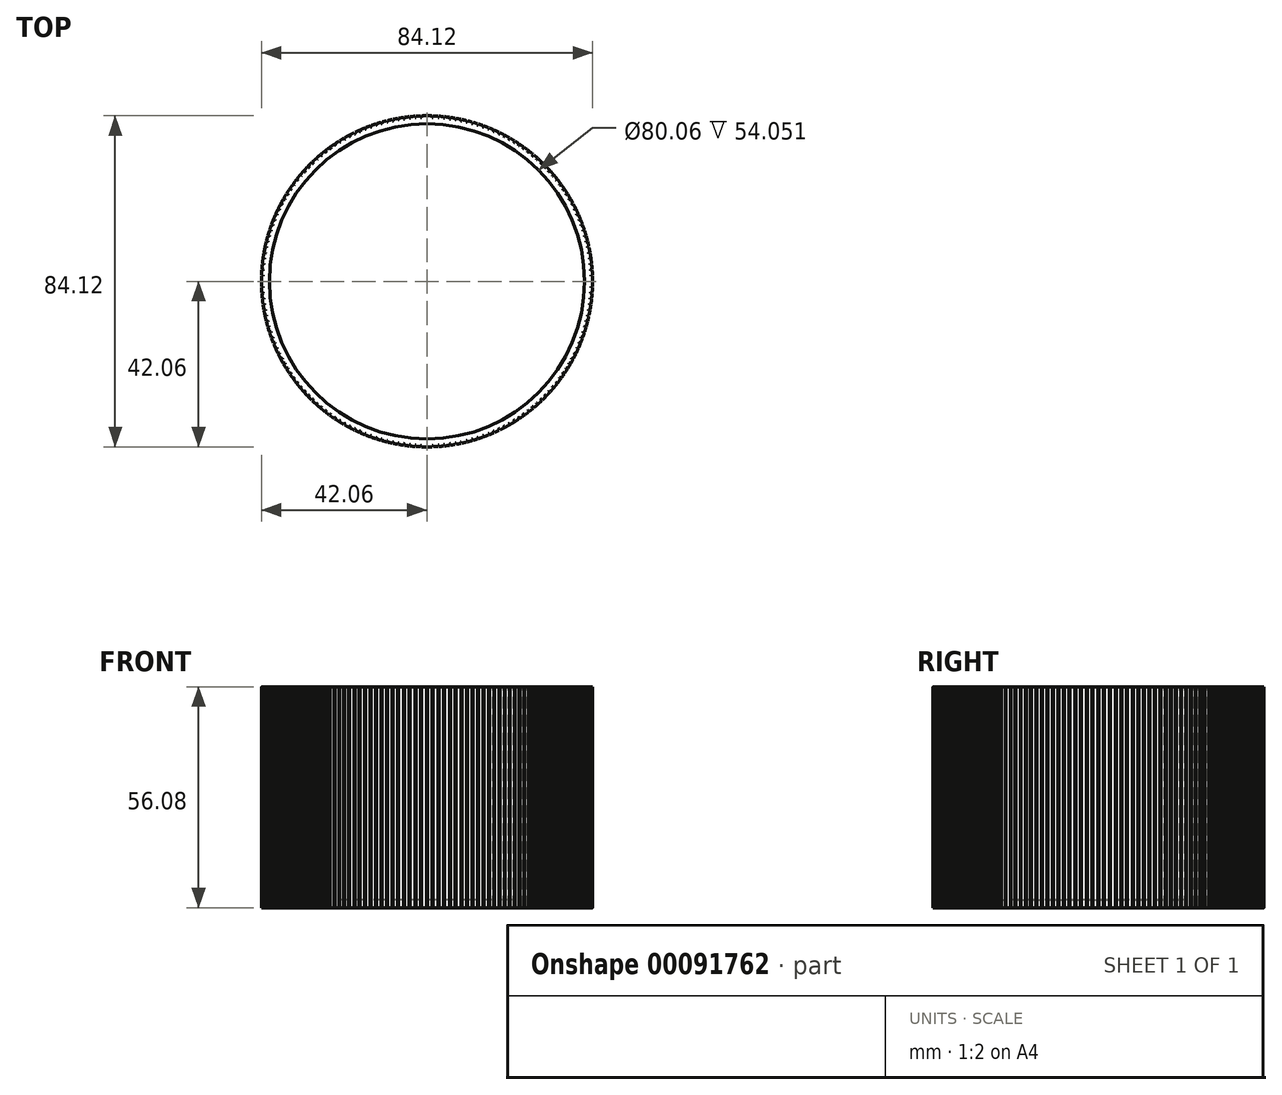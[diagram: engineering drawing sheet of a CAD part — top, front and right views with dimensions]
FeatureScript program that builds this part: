
annotation { "Feature Type Name" : "Feature", "Feature Type Description" : "" }
export const myFeature = defineFeature(function(context is Context, id is Id, definition is map)
    precondition{}
    {
        {
            var Q0;
            Q0=qCreatedBy(makeId("Top.planeOp"),FACE);
            var sketch = newSketch(context, id + "F0", { "sketchPlane" : qUnion([Q0])});
            skCircle(sketch, "E0", {"center": v(0, 0) * mm, "radius": 42.06 * mm});
            skSolve(sketch);
        }
        {
            var Q0;
            Q0 = qSketchRegion(id + "F0", true);
            extrude(context, id + "F1", {"entities" : qUnion([Q0]), "depth" : 56.08 * mm});
        }
        {
            var Q0;
            Q0=makeQuery(id+"F1.opExtrude","CAP_FACE",FACE,{"disambiguationData":[OSD([sQuery(id+"F0.wireOp",EDGE,"E0")])],"isStart":false});
            shell(context, id + "F2", {"entities" : qUnion([Q0]), "thickness" : 2.03 * mm});
        }
        {
            var Q0;
            Q0=makeQuery(id+"F1.opExtrude","CAP_FACE",FACE,{"disambiguationData":[OSD([sQuery(id+"F0.wireOp",EDGE,"E0")])],"isStart":false});
            var sketch = newSketch(context, id + "F3", { "sketchPlane" : qUnion([Q0])});
            skArc(sketch, "E1", {"start": v(0.13, 41.68) * mm, "mid": v(0, 41.68) * mm, "end": v(-0.13, 41.68) * mm});
            skLineSegment(sketch, "E2", {"start": v(-0.13, 41.68) * mm, "end": v(-0.13, 42.64) * mm});
            skLineSegment(sketch, "E3", {"start": v(-0.13, 42.64) * mm, "end": v(0.13, 42.64) * mm});
            skLineSegment(sketch, "E4", {"start": v(0.13, 42.64) * mm, "end": v(0.13, 41.68) * mm});
            skLineSegment(sketch, "E5.1.0", {"start": v(-1.58, 41.65) * mm, "end": v(-1.62, 42.6) * mm});
            skLineSegment(sketch, "E5.1.1", {"start": v(-1.36, 42.62) * mm, "end": v(-1.33, 41.66) * mm});
            skLineSegment(sketch, "E5.1.2", {"start": v(-1.62, 42.6) * mm, "end": v(-1.36, 42.62) * mm});
            skArc(sketch, "E5.1.3", {"start": v(-1.33, 41.66) * mm, "mid": v(-1.45, 41.66) * mm, "end": v(-1.58, 41.65) * mm});
            skLineSegment(sketch, "E5.2.0", {"start": v(-3.03, 41.57) * mm, "end": v(-3.1, 42.53) * mm});
            skLineSegment(sketch, "E5.2.1", {"start": v(-2.85, 42.54) * mm, "end": v(-2.78, 41.59) * mm});
            skLineSegment(sketch, "E5.2.2", {"start": v(-3.1, 42.53) * mm, "end": v(-2.85, 42.54) * mm});
            skArc(sketch, "E5.2.3", {"start": v(-2.78, 41.59) * mm, "mid": v(-2.9, 41.58) * mm, "end": v(-3.03, 41.57) * mm});
            skLineSegment(sketch, "E5.3.0", {"start": v(-4.48, 41.44) * mm, "end": v(-4.58, 42.4) * mm});
            skLineSegment(sketch, "E5.3.1", {"start": v(-4.33, 42.42) * mm, "end": v(-4.23, 41.47) * mm});
            skLineSegment(sketch, "E5.3.2", {"start": v(-4.58, 42.4) * mm, "end": v(-4.33, 42.42) * mm});
            skArc(sketch, "E5.3.3", {"start": v(-4.23, 41.47) * mm, "mid": v(-4.36, 41.45) * mm, "end": v(-4.48, 41.44) * mm});
            skLineSegment(sketch, "E5.4.0", {"start": v(-5.93, 41.26) * mm, "end": v(-6.06, 42.2) * mm});
            skLineSegment(sketch, "E5.4.1", {"start": v(-5.8, 42.24) * mm, "end": v(-5.68, 41.3) * mm});
            skLineSegment(sketch, "E5.4.2", {"start": v(-6.06, 42.2) * mm, "end": v(-5.8, 42.24) * mm});
            skArc(sketch, "E5.4.3", {"start": v(-5.68, 41.3) * mm, "mid": v(-5.8, 41.28) * mm, "end": v(-5.93, 41.26) * mm});
            skLineSegment(sketch, "E5.5.0", {"start": v(-7.36, 41.03) * mm, "end": v(-7.53, 41.97) * mm});
            skLineSegment(sketch, "E5.5.1", {"start": v(-7.28, 42.01) * mm, "end": v(-7.11, 41.07) * mm});
            skLineSegment(sketch, "E5.5.2", {"start": v(-7.53, 41.97) * mm, "end": v(-7.28, 42.01) * mm});
            skArc(sketch, "E5.5.3", {"start": v(-7.11, 41.07) * mm, "mid": v(-7.24, 41.05) * mm, "end": v(-7.36, 41.03) * mm});
            skLineSegment(sketch, "E5.6.0", {"start": v(-8.8, 40.74) * mm, "end": v(-8.99, 41.68) * mm});
            skLineSegment(sketch, "E5.6.1", {"start": v(-8.74, 41.73) * mm, "end": v(-8.54, 40.8) * mm});
            skLineSegment(sketch, "E5.6.2", {"start": v(-8.99, 41.68) * mm, "end": v(-8.74, 41.73) * mm});
            skArc(sketch, "E5.6.3", {"start": v(-8.54, 40.8) * mm, "mid": v(-8.67, 40.77) * mm, "end": v(-8.8, 40.74) * mm});
            skLineSegment(sketch, "E5.7.0", {"start": v(-10.2, 40.41) * mm, "end": v(-10.44, 41.34) * mm});
            skLineSegment(sketch, "E5.7.1", {"start": v(-10.2, 41.4) * mm, "end": v(-9.96, 40.47) * mm});
            skLineSegment(sketch, "E5.7.2", {"start": v(-10.44, 41.34) * mm, "end": v(-10.2, 41.4) * mm});
            skArc(sketch, "E5.7.3", {"start": v(-9.96, 40.47) * mm, "mid": v(-10.08, 40.44) * mm, "end": v(-10.2, 40.41) * mm});
            skLineSegment(sketch, "E5.8.0", {"start": v(-11.61, 40.03) * mm, "end": v(-11.87, 40.95) * mm});
            skLineSegment(sketch, "E5.8.1", {"start": v(-11.63, 41.02) * mm, "end": v(-11.37, 40.1) * mm});
            skLineSegment(sketch, "E5.8.2", {"start": v(-11.87, 40.95) * mm, "end": v(-11.63, 41.02) * mm});
            skArc(sketch, "E5.8.3", {"start": v(-11.37, 40.1) * mm, "mid": v(-11.49, 40.07) * mm, "end": v(-11.61, 40.03) * mm});
            skLineSegment(sketch, "E5.9.0", {"start": v(-13, 39.6) * mm, "end": v(-13.3, 40.51) * mm});
            skLineSegment(sketch, "E5.9.1", {"start": v(-13.06, 40.6) * mm, "end": v(-12.76, 39.68) * mm});
            skLineSegment(sketch, "E5.9.2", {"start": v(-13.3, 40.51) * mm, "end": v(-13.06, 40.6) * mm});
            skArc(sketch, "E5.9.3", {"start": v(-12.76, 39.68) * mm, "mid": v(-12.88, 39.64) * mm, "end": v(-13, 39.6) * mm});
            skLineSegment(sketch, "E5.10.0", {"start": v(-14.38, 39.12) * mm, "end": v(-14.7, 40.02) * mm});
            skLineSegment(sketch, "E5.10.1", {"start": v(-14.46, 40.11) * mm, "end": v(-14.14, 39.21) * mm});
            skLineSegment(sketch, "E5.10.2", {"start": v(-14.7, 40.02) * mm, "end": v(-14.46, 40.11) * mm});
            skArc(sketch, "E5.10.3", {"start": v(-14.14, 39.21) * mm, "mid": v(-14.26, 39.17) * mm, "end": v(-14.38, 39.12) * mm});
            skLineSegment(sketch, "E5.11.0", {"start": v(-15.73, 38.6) * mm, "end": v(-16.1, 39.49) * mm});
            skLineSegment(sketch, "E5.11.1", {"start": v(-15.86, 39.58) * mm, "end": v(-15.5, 38.7) * mm});
            skLineSegment(sketch, "E5.11.2", {"start": v(-16.1, 39.49) * mm, "end": v(-15.86, 39.58) * mm});
            skArc(sketch, "E5.11.3", {"start": v(-15.5, 38.7) * mm, "mid": v(-15.61, 38.65) * mm, "end": v(-15.73, 38.6) * mm});
            skLineSegment(sketch, "E5.12.0", {"start": v(-17.07, 38.03) * mm, "end": v(-17.46, 38.9) * mm});
            skLineSegment(sketch, "E5.12.1", {"start": v(-17.23, 39) * mm, "end": v(-16.84, 38.13) * mm});
            skLineSegment(sketch, "E5.12.2", {"start": v(-17.46, 38.9) * mm, "end": v(-17.23, 39) * mm});
            skArc(sketch, "E5.12.3", {"start": v(-16.84, 38.13) * mm, "mid": v(-16.95, 38.08) * mm, "end": v(-17.07, 38.03) * mm});
            skLineSegment(sketch, "E5.13.0", {"start": v(-18.39, 37.4) * mm, "end": v(-18.8, 38.27) * mm});
            skLineSegment(sketch, "E5.13.1", {"start": v(-18.58, 38.38) * mm, "end": v(-18.16, 37.52) * mm});
            skLineSegment(sketch, "E5.13.2", {"start": v(-18.8, 38.27) * mm, "end": v(-18.58, 38.38) * mm});
            skArc(sketch, "E5.13.3", {"start": v(-18.16, 37.52) * mm, "mid": v(-18.27, 37.46) * mm, "end": v(-18.39, 37.4) * mm});
            skLineSegment(sketch, "E5.14.0", {"start": v(-19.68, 36.74) * mm, "end": v(-20.13, 37.59) * mm});
            skLineSegment(sketch, "E5.14.1", {"start": v(-19.9, 37.7) * mm, "end": v(-19.46, 36.86) * mm});
            skLineSegment(sketch, "E5.14.2", {"start": v(-20.13, 37.59) * mm, "end": v(-19.9, 37.7) * mm});
            skArc(sketch, "E5.14.3", {"start": v(-19.46, 36.86) * mm, "mid": v(-19.57, 36.8) * mm, "end": v(-19.68, 36.74) * mm});
            skLineSegment(sketch, "E5.15.0", {"start": v(-20.95, 36.03) * mm, "end": v(-21.43, 36.86) * mm});
            skLineSegment(sketch, "E5.15.1", {"start": v(-21.2, 36.99) * mm, "end": v(-20.73, 36.16) * mm});
            skLineSegment(sketch, "E5.15.2", {"start": v(-21.43, 36.86) * mm, "end": v(-21.2, 36.99) * mm});
            skArc(sketch, "E5.15.3", {"start": v(-20.73, 36.16) * mm, "mid": v(-20.84, 36.1) * mm, "end": v(-20.95, 36.03) * mm});
            skLineSegment(sketch, "E5.16.0", {"start": v(-22.2, 35.28) * mm, "end": v(-22.7, 36.1) * mm});
            skLineSegment(sketch, "E5.16.1", {"start": v(-22.49, 36.23) * mm, "end": v(-21.98, 35.41) * mm});
            skLineSegment(sketch, "E5.16.2", {"start": v(-22.7, 36.1) * mm, "end": v(-22.49, 36.23) * mm});
            skArc(sketch, "E5.16.3", {"start": v(-21.98, 35.41) * mm, "mid": v(-22.09, 35.35) * mm, "end": v(-22.2, 35.28) * mm});
            skLineSegment(sketch, "E5.17.0", {"start": v(-23.41, 34.48) * mm, "end": v(-23.95, 35.28) * mm});
            skLineSegment(sketch, "E5.17.1", {"start": v(-23.74, 35.42) * mm, "end": v(-23.2, 34.63) * mm});
            skLineSegment(sketch, "E5.17.2", {"start": v(-23.95, 35.28) * mm, "end": v(-23.74, 35.42) * mm});
            skArc(sketch, "E5.17.3", {"start": v(-23.2, 34.63) * mm, "mid": v(-23.3, 34.56) * mm, "end": v(-23.41, 34.48) * mm});
            skLineSegment(sketch, "E5.18.0", {"start": v(-24.6, 33.65) * mm, "end": v(-25.17, 34.42) * mm});
            skLineSegment(sketch, "E5.18.1", {"start": v(-24.96, 34.57) * mm, "end": v(-24.4, 33.8) * mm});
            skLineSegment(sketch, "E5.18.2", {"start": v(-25.17, 34.42) * mm, "end": v(-24.96, 34.57) * mm});
            skArc(sketch, "E5.18.3", {"start": v(-24.4, 33.8) * mm, "mid": v(-24.5, 33.72) * mm, "end": v(-24.6, 33.65) * mm});
            skLineSegment(sketch, "E5.19.0", {"start": v(-25.76, 32.77) * mm, "end": v(-26.35, 33.52) * mm});
            skLineSegment(sketch, "E5.19.1", {"start": v(-26.15, 33.68) * mm, "end": v(-25.56, 32.92) * mm});
            skLineSegment(sketch, "E5.19.2", {"start": v(-26.35, 33.52) * mm, "end": v(-26.15, 33.68) * mm});
            skArc(sketch, "E5.19.3", {"start": v(-25.56, 32.92) * mm, "mid": v(-25.66, 32.85) * mm, "end": v(-25.76, 32.77) * mm});
            skLineSegment(sketch, "E5.20.0", {"start": v(-26.89, 31.85) * mm, "end": v(-27.5, 32.58) * mm});
            skLineSegment(sketch, "E5.20.1", {"start": v(-27.31, 32.74) * mm, "end": v(-26.7, 32.01) * mm});
            skLineSegment(sketch, "E5.20.2", {"start": v(-27.5, 32.58) * mm, "end": v(-27.31, 32.74) * mm});
            skArc(sketch, "E5.20.3", {"start": v(-26.7, 32.01) * mm, "mid": v(-26.8, 31.93) * mm, "end": v(-26.89, 31.85) * mm});
            skLineSegment(sketch, "E5.21.0", {"start": v(-27.98, 30.9) * mm, "end": v(-28.63, 31.6) * mm});
            skLineSegment(sketch, "E5.21.1", {"start": v(-28.44, 31.77) * mm, "end": v(-27.8, 31.06) * mm});
            skLineSegment(sketch, "E5.21.2", {"start": v(-28.63, 31.6) * mm, "end": v(-28.44, 31.77) * mm});
            skArc(sketch, "E5.21.3", {"start": v(-27.8, 31.06) * mm, "mid": v(-27.9, 30.98) * mm, "end": v(-27.98, 30.9) * mm});
            skLineSegment(sketch, "E5.22.0", {"start": v(-29.05, 29.9) * mm, "end": v(-29.71, 30.58) * mm});
            skLineSegment(sketch, "E5.22.1", {"start": v(-29.53, 30.76) * mm, "end": v(-28.86, 30.07) * mm});
            skLineSegment(sketch, "E5.22.2", {"start": v(-29.71, 30.58) * mm, "end": v(-29.53, 30.76) * mm});
            skArc(sketch, "E5.22.3", {"start": v(-28.86, 30.07) * mm, "mid": v(-28.95, 29.98) * mm, "end": v(-29.05, 29.9) * mm});
            skLineSegment(sketch, "E5.23.0", {"start": v(-30.07, 28.86) * mm, "end": v(-30.76, 29.53) * mm});
            skLineSegment(sketch, "E5.23.1", {"start": v(-30.58, 29.71) * mm, "end": v(-29.9, 29.05) * mm});
            skLineSegment(sketch, "E5.23.2", {"start": v(-30.76, 29.53) * mm, "end": v(-30.58, 29.71) * mm});
            skArc(sketch, "E5.23.3", {"start": v(-29.9, 29.05) * mm, "mid": v(-29.98, 28.95) * mm, "end": v(-30.07, 28.86) * mm});
            skLineSegment(sketch, "E5.24.0", {"start": v(-31.06, 27.8) * mm, "end": v(-31.77, 28.44) * mm});
            skLineSegment(sketch, "E5.24.1", {"start": v(-31.6, 28.63) * mm, "end": v(-30.9, 27.98) * mm});
            skLineSegment(sketch, "E5.24.2", {"start": v(-31.77, 28.44) * mm, "end": v(-31.6, 28.63) * mm});
            skArc(sketch, "E5.24.3", {"start": v(-30.9, 27.98) * mm, "mid": v(-30.98, 27.9) * mm, "end": v(-31.06, 27.8) * mm});
            skLineSegment(sketch, "E5.25.0", {"start": v(-32.01, 26.7) * mm, "end": v(-32.74, 27.31) * mm});
            skLineSegment(sketch, "E5.25.1", {"start": v(-32.58, 27.5) * mm, "end": v(-31.85, 26.89) * mm});
            skLineSegment(sketch, "E5.25.2", {"start": v(-32.74, 27.31) * mm, "end": v(-32.58, 27.5) * mm});
            skArc(sketch, "E5.25.3", {"start": v(-31.85, 26.89) * mm, "mid": v(-31.93, 26.8) * mm, "end": v(-32.01, 26.7) * mm});
            skLineSegment(sketch, "E5.26.0", {"start": v(-32.92, 25.56) * mm, "end": v(-33.68, 26.15) * mm});
            skLineSegment(sketch, "E5.26.1", {"start": v(-33.52, 26.35) * mm, "end": v(-32.77, 25.76) * mm});
            skLineSegment(sketch, "E5.26.2", {"start": v(-33.68, 26.15) * mm, "end": v(-33.52, 26.35) * mm});
            skArc(sketch, "E5.26.3", {"start": v(-32.77, 25.76) * mm, "mid": v(-32.85, 25.66) * mm, "end": v(-32.92, 25.56) * mm});
            skLineSegment(sketch, "E5.27.0", {"start": v(-33.8, 24.4) * mm, "end": v(-34.57, 24.96) * mm});
            skLineSegment(sketch, "E5.27.1", {"start": v(-34.42, 25.17) * mm, "end": v(-33.65, 24.6) * mm});
            skLineSegment(sketch, "E5.27.2", {"start": v(-34.57, 24.96) * mm, "end": v(-34.42, 25.17) * mm});
            skArc(sketch, "E5.27.3", {"start": v(-33.65, 24.6) * mm, "mid": v(-33.72, 24.5) * mm, "end": v(-33.8, 24.4) * mm});
            skLineSegment(sketch, "E5.28.0", {"start": v(-34.63, 23.2) * mm, "end": v(-35.42, 23.74) * mm});
            skLineSegment(sketch, "E5.28.1", {"start": v(-35.28, 23.95) * mm, "end": v(-34.48, 23.41) * mm});
            skLineSegment(sketch, "E5.28.2", {"start": v(-35.42, 23.74) * mm, "end": v(-35.28, 23.95) * mm});
            skArc(sketch, "E5.28.3", {"start": v(-34.48, 23.41) * mm, "mid": v(-34.56, 23.3) * mm, "end": v(-34.63, 23.2) * mm});
            skLineSegment(sketch, "E5.29.0", {"start": v(-35.41, 21.98) * mm, "end": v(-36.23, 22.49) * mm});
            skLineSegment(sketch, "E5.29.1", {"start": v(-36.1, 22.7) * mm, "end": v(-35.28, 22.2) * mm});
            skLineSegment(sketch, "E5.29.2", {"start": v(-36.23, 22.49) * mm, "end": v(-36.1, 22.7) * mm});
            skArc(sketch, "E5.29.3", {"start": v(-35.28, 22.2) * mm, "mid": v(-35.35, 22.09) * mm, "end": v(-35.41, 21.98) * mm});
            skLineSegment(sketch, "E5.30.0", {"start": v(-36.16, 20.73) * mm, "end": v(-36.99, 21.2) * mm});
            skLineSegment(sketch, "E5.30.1", {"start": v(-36.86, 21.43) * mm, "end": v(-36.03, 20.95) * mm});
            skLineSegment(sketch, "E5.30.2", {"start": v(-36.99, 21.2) * mm, "end": v(-36.86, 21.43) * mm});
            skArc(sketch, "E5.30.3", {"start": v(-36.03, 20.95) * mm, "mid": v(-36.1, 20.84) * mm, "end": v(-36.16, 20.73) * mm});
            skLineSegment(sketch, "E5.31.0", {"start": v(-36.86, 19.46) * mm, "end": v(-37.7, 19.9) * mm});
            skLineSegment(sketch, "E5.31.1", {"start": v(-37.59, 20.13) * mm, "end": v(-36.74, 19.68) * mm});
            skLineSegment(sketch, "E5.31.2", {"start": v(-37.7, 19.9) * mm, "end": v(-37.59, 20.13) * mm});
            skArc(sketch, "E5.31.3", {"start": v(-36.74, 19.68) * mm, "mid": v(-36.8, 19.57) * mm, "end": v(-36.86, 19.46) * mm});
            skLineSegment(sketch, "E5.32.0", {"start": v(-37.52, 18.16) * mm, "end": v(-38.38, 18.58) * mm});
            skLineSegment(sketch, "E5.32.1", {"start": v(-38.27, 18.8) * mm, "end": v(-37.4, 18.39) * mm});
            skLineSegment(sketch, "E5.32.2", {"start": v(-38.38, 18.58) * mm, "end": v(-38.27, 18.8) * mm});
            skArc(sketch, "E5.32.3", {"start": v(-37.4, 18.39) * mm, "mid": v(-37.46, 18.27) * mm, "end": v(-37.52, 18.16) * mm});
            skLineSegment(sketch, "E5.33.0", {"start": v(-38.13, 16.84) * mm, "end": v(-39, 17.23) * mm});
            skLineSegment(sketch, "E5.33.1", {"start": v(-38.9, 17.46) * mm, "end": v(-38.03, 17.07) * mm});
            skLineSegment(sketch, "E5.33.2", {"start": v(-39, 17.23) * mm, "end": v(-38.9, 17.46) * mm});
            skArc(sketch, "E5.33.3", {"start": v(-38.03, 17.07) * mm, "mid": v(-38.08, 16.95) * mm, "end": v(-38.13, 16.84) * mm});
            skLineSegment(sketch, "E5.34.0", {"start": v(-38.7, 15.5) * mm, "end": v(-39.58, 15.86) * mm});
            skLineSegment(sketch, "E5.34.1", {"start": v(-39.49, 16.1) * mm, "end": v(-38.6, 15.73) * mm});
            skLineSegment(sketch, "E5.34.2", {"start": v(-39.58, 15.86) * mm, "end": v(-39.49, 16.1) * mm});
            skArc(sketch, "E5.34.3", {"start": v(-38.6, 15.73) * mm, "mid": v(-38.65, 15.61) * mm, "end": v(-38.7, 15.5) * mm});
            skLineSegment(sketch, "E5.35.0", {"start": v(-39.21, 14.14) * mm, "end": v(-40.11, 14.46) * mm});
            skLineSegment(sketch, "E5.35.1", {"start": v(-40.02, 14.7) * mm, "end": v(-39.12, 14.38) * mm});
            skLineSegment(sketch, "E5.35.2", {"start": v(-40.11, 14.46) * mm, "end": v(-40.02, 14.7) * mm});
            skArc(sketch, "E5.35.3", {"start": v(-39.12, 14.38) * mm, "mid": v(-39.17, 14.26) * mm, "end": v(-39.21, 14.14) * mm});
            skLineSegment(sketch, "E5.36.0", {"start": v(-39.68, 12.76) * mm, "end": v(-40.6, 13.06) * mm});
            skLineSegment(sketch, "E5.36.1", {"start": v(-40.51, 13.3) * mm, "end": v(-39.6, 13) * mm});
            skLineSegment(sketch, "E5.36.2", {"start": v(-40.6, 13.06) * mm, "end": v(-40.51, 13.3) * mm});
            skArc(sketch, "E5.36.3", {"start": v(-39.6, 13) * mm, "mid": v(-39.64, 12.88) * mm, "end": v(-39.68, 12.76) * mm});
            skLineSegment(sketch, "E5.37.0", {"start": v(-40.1, 11.37) * mm, "end": v(-41.02, 11.63) * mm});
            skLineSegment(sketch, "E5.37.1", {"start": v(-40.95, 11.87) * mm, "end": v(-40.03, 11.61) * mm});
            skLineSegment(sketch, "E5.37.2", {"start": v(-41.02, 11.63) * mm, "end": v(-40.95, 11.87) * mm});
            skArc(sketch, "E5.37.3", {"start": v(-40.03, 11.61) * mm, "mid": v(-40.07, 11.49) * mm, "end": v(-40.1, 11.37) * mm});
            skLineSegment(sketch, "E5.38.0", {"start": v(-40.47, 9.96) * mm, "end": v(-41.4, 10.2) * mm});
            skLineSegment(sketch, "E5.38.1", {"start": v(-41.34, 10.44) * mm, "end": v(-40.41, 10.2) * mm});
            skLineSegment(sketch, "E5.38.2", {"start": v(-41.4, 10.2) * mm, "end": v(-41.34, 10.44) * mm});
            skArc(sketch, "E5.38.3", {"start": v(-40.41, 10.2) * mm, "mid": v(-40.44, 10.08) * mm, "end": v(-40.47, 9.96) * mm});
            skLineSegment(sketch, "E5.39.0", {"start": v(-40.8, 8.54) * mm, "end": v(-41.73, 8.74) * mm});
            skLineSegment(sketch, "E5.39.1", {"start": v(-41.68, 8.99) * mm, "end": v(-40.74, 8.8) * mm});
            skLineSegment(sketch, "E5.39.2", {"start": v(-41.73, 8.74) * mm, "end": v(-41.68, 8.99) * mm});
            skArc(sketch, "E5.39.3", {"start": v(-40.74, 8.8) * mm, "mid": v(-40.77, 8.67) * mm, "end": v(-40.8, 8.54) * mm});
            skLineSegment(sketch, "E5.40.0", {"start": v(-41.07, 7.11) * mm, "end": v(-42.01, 7.28) * mm});
            skLineSegment(sketch, "E5.40.1", {"start": v(-41.97, 7.53) * mm, "end": v(-41.03, 7.36) * mm});
            skLineSegment(sketch, "E5.40.2", {"start": v(-42.01, 7.28) * mm, "end": v(-41.97, 7.53) * mm});
            skArc(sketch, "E5.40.3", {"start": v(-41.03, 7.36) * mm, "mid": v(-41.05, 7.24) * mm, "end": v(-41.07, 7.11) * mm});
            skLineSegment(sketch, "E5.41.0", {"start": v(-41.3, 5.68) * mm, "end": v(-42.24, 5.8) * mm});
            skLineSegment(sketch, "E5.41.1", {"start": v(-42.2, 6.06) * mm, "end": v(-41.26, 5.93) * mm});
            skLineSegment(sketch, "E5.41.2", {"start": v(-42.24, 5.8) * mm, "end": v(-42.2, 6.06) * mm});
            skArc(sketch, "E5.41.3", {"start": v(-41.26, 5.93) * mm, "mid": v(-41.28, 5.8) * mm, "end": v(-41.3, 5.68) * mm});
            skLineSegment(sketch, "E5.42.0", {"start": v(-41.47, 4.23) * mm, "end": v(-42.42, 4.33) * mm});
            skLineSegment(sketch, "E5.42.1", {"start": v(-42.4, 4.58) * mm, "end": v(-41.44, 4.48) * mm});
            skLineSegment(sketch, "E5.42.2", {"start": v(-42.42, 4.33) * mm, "end": v(-42.4, 4.58) * mm});
            skArc(sketch, "E5.42.3", {"start": v(-41.44, 4.48) * mm, "mid": v(-41.45, 4.36) * mm, "end": v(-41.47, 4.23) * mm});
            skLineSegment(sketch, "E5.43.0", {"start": v(-41.59, 2.78) * mm, "end": v(-42.54, 2.85) * mm});
            skLineSegment(sketch, "E5.43.1", {"start": v(-42.53, 3.1) * mm, "end": v(-41.57, 3.03) * mm});
            skLineSegment(sketch, "E5.43.2", {"start": v(-42.54, 2.85) * mm, "end": v(-42.53, 3.1) * mm});
            skArc(sketch, "E5.43.3", {"start": v(-41.57, 3.03) * mm, "mid": v(-41.58, 2.9) * mm, "end": v(-41.59, 2.78) * mm});
            skLineSegment(sketch, "E5.44.0", {"start": v(-41.66, 1.33) * mm, "end": v(-42.62, 1.36) * mm});
            skLineSegment(sketch, "E5.44.1", {"start": v(-42.6, 1.62) * mm, "end": v(-41.65, 1.58) * mm});
            skLineSegment(sketch, "E5.44.2", {"start": v(-42.62, 1.36) * mm, "end": v(-42.6, 1.62) * mm});
            skArc(sketch, "E5.44.3", {"start": v(-41.65, 1.58) * mm, "mid": v(-41.66, 1.45) * mm, "end": v(-41.66, 1.33) * mm});
            skLineSegment(sketch, "E5.45.0", {"start": v(-41.68, -0.13) * mm, "end": v(-42.64, -0.13) * mm});
            skLineSegment(sketch, "E5.45.1", {"start": v(-42.64, 0.13) * mm, "end": v(-41.68, 0.13) * mm});
            skLineSegment(sketch, "E5.45.2", {"start": v(-42.64, -0.13) * mm, "end": v(-42.64, 0.13) * mm});
            skArc(sketch, "E5.45.3", {"start": v(-41.68, 0.13) * mm, "mid": v(-41.68, 0) * mm, "end": v(-41.68, -0.13) * mm});
            skLineSegment(sketch, "E5.46.0", {"start": v(-41.65, -1.58) * mm, "end": v(-42.6, -1.62) * mm});
            skLineSegment(sketch, "E5.46.1", {"start": v(-42.62, -1.36) * mm, "end": v(-41.66, -1.33) * mm});
            skLineSegment(sketch, "E5.46.2", {"start": v(-42.6, -1.62) * mm, "end": v(-42.62, -1.36) * mm});
            skArc(sketch, "E5.46.3", {"start": v(-41.66, -1.33) * mm, "mid": v(-41.66, -1.45) * mm, "end": v(-41.65, -1.58) * mm});
            skLineSegment(sketch, "E5.47.0", {"start": v(-41.57, -3.03) * mm, "end": v(-42.53, -3.1) * mm});
            skLineSegment(sketch, "E5.47.1", {"start": v(-42.54, -2.85) * mm, "end": v(-41.59, -2.78) * mm});
            skLineSegment(sketch, "E5.47.2", {"start": v(-42.53, -3.1) * mm, "end": v(-42.54, -2.85) * mm});
            skArc(sketch, "E5.47.3", {"start": v(-41.59, -2.78) * mm, "mid": v(-41.58, -2.9) * mm, "end": v(-41.57, -3.03) * mm});
            skLineSegment(sketch, "E5.48.0", {"start": v(-41.44, -4.48) * mm, "end": v(-42.4, -4.58) * mm});
            skLineSegment(sketch, "E5.48.1", {"start": v(-42.42, -4.33) * mm, "end": v(-41.47, -4.23) * mm});
            skLineSegment(sketch, "E5.48.2", {"start": v(-42.4, -4.58) * mm, "end": v(-42.42, -4.33) * mm});
            skArc(sketch, "E5.48.3", {"start": v(-41.47, -4.23) * mm, "mid": v(-41.45, -4.36) * mm, "end": v(-41.44, -4.48) * mm});
            skLineSegment(sketch, "E5.49.0", {"start": v(-41.26, -5.93) * mm, "end": v(-42.2, -6.06) * mm});
            skLineSegment(sketch, "E5.49.1", {"start": v(-42.24, -5.8) * mm, "end": v(-41.3, -5.68) * mm});
            skLineSegment(sketch, "E5.49.2", {"start": v(-42.2, -6.06) * mm, "end": v(-42.24, -5.8) * mm});
            skArc(sketch, "E5.49.3", {"start": v(-41.3, -5.68) * mm, "mid": v(-41.28, -5.8) * mm, "end": v(-41.26, -5.93) * mm});
            skLineSegment(sketch, "E5.50.0", {"start": v(-41.03, -7.36) * mm, "end": v(-41.97, -7.53) * mm});
            skLineSegment(sketch, "E5.50.1", {"start": v(-42.01, -7.28) * mm, "end": v(-41.07, -7.11) * mm});
            skLineSegment(sketch, "E5.50.2", {"start": v(-41.97, -7.53) * mm, "end": v(-42.01, -7.28) * mm});
            skArc(sketch, "E5.50.3", {"start": v(-41.07, -7.11) * mm, "mid": v(-41.05, -7.24) * mm, "end": v(-41.03, -7.36) * mm});
            skLineSegment(sketch, "E5.51.0", {"start": v(-40.74, -8.8) * mm, "end": v(-41.68, -8.99) * mm});
            skLineSegment(sketch, "E5.51.1", {"start": v(-41.73, -8.74) * mm, "end": v(-40.8, -8.54) * mm});
            skLineSegment(sketch, "E5.51.2", {"start": v(-41.68, -8.99) * mm, "end": v(-41.73, -8.74) * mm});
            skArc(sketch, "E5.51.3", {"start": v(-40.8, -8.54) * mm, "mid": v(-40.77, -8.67) * mm, "end": v(-40.74, -8.8) * mm});
            skLineSegment(sketch, "E5.52.0", {"start": v(-40.41, -10.2) * mm, "end": v(-41.34, -10.44) * mm});
            skLineSegment(sketch, "E5.52.1", {"start": v(-41.4, -10.2) * mm, "end": v(-40.47, -9.96) * mm});
            skLineSegment(sketch, "E5.52.2", {"start": v(-41.34, -10.44) * mm, "end": v(-41.4, -10.2) * mm});
            skArc(sketch, "E5.52.3", {"start": v(-40.47, -9.96) * mm, "mid": v(-40.44, -10.08) * mm, "end": v(-40.41, -10.2) * mm});
            skLineSegment(sketch, "E5.53.0", {"start": v(-40.03, -11.61) * mm, "end": v(-40.95, -11.87) * mm});
            skLineSegment(sketch, "E5.53.1", {"start": v(-41.02, -11.63) * mm, "end": v(-40.1, -11.37) * mm});
            skLineSegment(sketch, "E5.53.2", {"start": v(-40.95, -11.87) * mm, "end": v(-41.02, -11.63) * mm});
            skArc(sketch, "E5.53.3", {"start": v(-40.1, -11.37) * mm, "mid": v(-40.07, -11.49) * mm, "end": v(-40.03, -11.61) * mm});
            skLineSegment(sketch, "E5.54.0", {"start": v(-39.6, -13) * mm, "end": v(-40.51, -13.3) * mm});
            skLineSegment(sketch, "E5.54.1", {"start": v(-40.6, -13.06) * mm, "end": v(-39.68, -12.76) * mm});
            skLineSegment(sketch, "E5.54.2", {"start": v(-40.51, -13.3) * mm, "end": v(-40.6, -13.06) * mm});
            skArc(sketch, "E5.54.3", {"start": v(-39.68, -12.76) * mm, "mid": v(-39.64, -12.88) * mm, "end": v(-39.6, -13) * mm});
            skLineSegment(sketch, "E5.55.0", {"start": v(-39.12, -14.38) * mm, "end": v(-40.02, -14.7) * mm});
            skLineSegment(sketch, "E5.55.1", {"start": v(-40.11, -14.46) * mm, "end": v(-39.21, -14.14) * mm});
            skLineSegment(sketch, "E5.55.2", {"start": v(-40.02, -14.7) * mm, "end": v(-40.11, -14.46) * mm});
            skArc(sketch, "E5.55.3", {"start": v(-39.21, -14.14) * mm, "mid": v(-39.17, -14.26) * mm, "end": v(-39.12, -14.38) * mm});
            skLineSegment(sketch, "E5.56.0", {"start": v(-38.6, -15.73) * mm, "end": v(-39.49, -16.1) * mm});
            skLineSegment(sketch, "E5.56.1", {"start": v(-39.58, -15.86) * mm, "end": v(-38.7, -15.5) * mm});
            skLineSegment(sketch, "E5.56.2", {"start": v(-39.49, -16.1) * mm, "end": v(-39.58, -15.86) * mm});
            skArc(sketch, "E5.56.3", {"start": v(-38.7, -15.5) * mm, "mid": v(-38.65, -15.61) * mm, "end": v(-38.6, -15.73) * mm});
            skLineSegment(sketch, "E5.57.0", {"start": v(-38.03, -17.07) * mm, "end": v(-38.9, -17.46) * mm});
            skLineSegment(sketch, "E5.57.1", {"start": v(-39, -17.23) * mm, "end": v(-38.13, -16.84) * mm});
            skLineSegment(sketch, "E5.57.2", {"start": v(-38.9, -17.46) * mm, "end": v(-39, -17.23) * mm});
            skArc(sketch, "E5.57.3", {"start": v(-38.13, -16.84) * mm, "mid": v(-38.08, -16.95) * mm, "end": v(-38.03, -17.07) * mm});
            skLineSegment(sketch, "E5.58.0", {"start": v(-37.4, -18.39) * mm, "end": v(-38.27, -18.8) * mm});
            skLineSegment(sketch, "E5.58.1", {"start": v(-38.38, -18.58) * mm, "end": v(-37.52, -18.16) * mm});
            skLineSegment(sketch, "E5.58.2", {"start": v(-38.27, -18.8) * mm, "end": v(-38.38, -18.58) * mm});
            skArc(sketch, "E5.58.3", {"start": v(-37.52, -18.16) * mm, "mid": v(-37.46, -18.27) * mm, "end": v(-37.4, -18.39) * mm});
            skLineSegment(sketch, "E5.59.0", {"start": v(-36.74, -19.68) * mm, "end": v(-37.59, -20.13) * mm});
            skLineSegment(sketch, "E5.59.1", {"start": v(-37.7, -19.9) * mm, "end": v(-36.86, -19.46) * mm});
            skLineSegment(sketch, "E5.59.2", {"start": v(-37.59, -20.13) * mm, "end": v(-37.7, -19.9) * mm});
            skArc(sketch, "E5.59.3", {"start": v(-36.86, -19.46) * mm, "mid": v(-36.8, -19.57) * mm, "end": v(-36.74, -19.68) * mm});
            skLineSegment(sketch, "E5.60.0", {"start": v(-36.03, -20.95) * mm, "end": v(-36.86, -21.43) * mm});
            skLineSegment(sketch, "E5.60.1", {"start": v(-36.99, -21.2) * mm, "end": v(-36.16, -20.73) * mm});
            skLineSegment(sketch, "E5.60.2", {"start": v(-36.86, -21.43) * mm, "end": v(-36.99, -21.2) * mm});
            skArc(sketch, "E5.60.3", {"start": v(-36.16, -20.73) * mm, "mid": v(-36.1, -20.84) * mm, "end": v(-36.03, -20.95) * mm});
            skLineSegment(sketch, "E5.61.0", {"start": v(-35.28, -22.2) * mm, "end": v(-36.1, -22.7) * mm});
            skLineSegment(sketch, "E5.61.1", {"start": v(-36.23, -22.49) * mm, "end": v(-35.41, -21.98) * mm});
            skLineSegment(sketch, "E5.61.2", {"start": v(-36.1, -22.7) * mm, "end": v(-36.23, -22.49) * mm});
            skArc(sketch, "E5.61.3", {"start": v(-35.41, -21.98) * mm, "mid": v(-35.35, -22.09) * mm, "end": v(-35.28, -22.2) * mm});
            skLineSegment(sketch, "E5.62.0", {"start": v(-34.48, -23.41) * mm, "end": v(-35.28, -23.95) * mm});
            skLineSegment(sketch, "E5.62.1", {"start": v(-35.42, -23.74) * mm, "end": v(-34.63, -23.2) * mm});
            skLineSegment(sketch, "E5.62.2", {"start": v(-35.28, -23.95) * mm, "end": v(-35.42, -23.74) * mm});
            skArc(sketch, "E5.62.3", {"start": v(-34.63, -23.2) * mm, "mid": v(-34.56, -23.3) * mm, "end": v(-34.48, -23.41) * mm});
            skLineSegment(sketch, "E5.63.0", {"start": v(-33.65, -24.6) * mm, "end": v(-34.42, -25.17) * mm});
            skLineSegment(sketch, "E5.63.1", {"start": v(-34.57, -24.96) * mm, "end": v(-33.8, -24.4) * mm});
            skLineSegment(sketch, "E5.63.2", {"start": v(-34.42, -25.17) * mm, "end": v(-34.57, -24.96) * mm});
            skArc(sketch, "E5.63.3", {"start": v(-33.8, -24.4) * mm, "mid": v(-33.72, -24.5) * mm, "end": v(-33.65, -24.6) * mm});
            skLineSegment(sketch, "E5.64.0", {"start": v(-32.77, -25.76) * mm, "end": v(-33.52, -26.35) * mm});
            skLineSegment(sketch, "E5.64.1", {"start": v(-33.68, -26.15) * mm, "end": v(-32.92, -25.56) * mm});
            skLineSegment(sketch, "E5.64.2", {"start": v(-33.52, -26.35) * mm, "end": v(-33.68, -26.15) * mm});
            skArc(sketch, "E5.64.3", {"start": v(-32.92, -25.56) * mm, "mid": v(-32.85, -25.66) * mm, "end": v(-32.77, -25.76) * mm});
            skLineSegment(sketch, "E5.65.0", {"start": v(-31.85, -26.89) * mm, "end": v(-32.58, -27.5) * mm});
            skLineSegment(sketch, "E5.65.1", {"start": v(-32.74, -27.31) * mm, "end": v(-32.01, -26.7) * mm});
            skLineSegment(sketch, "E5.65.2", {"start": v(-32.58, -27.5) * mm, "end": v(-32.74, -27.31) * mm});
            skArc(sketch, "E5.65.3", {"start": v(-32.01, -26.7) * mm, "mid": v(-31.93, -26.8) * mm, "end": v(-31.85, -26.89) * mm});
            skLineSegment(sketch, "E5.66.0", {"start": v(-30.9, -27.98) * mm, "end": v(-31.6, -28.63) * mm});
            skLineSegment(sketch, "E5.66.1", {"start": v(-31.77, -28.44) * mm, "end": v(-31.06, -27.8) * mm});
            skLineSegment(sketch, "E5.66.2", {"start": v(-31.6, -28.63) * mm, "end": v(-31.77, -28.44) * mm});
            skArc(sketch, "E5.66.3", {"start": v(-31.06, -27.8) * mm, "mid": v(-30.98, -27.9) * mm, "end": v(-30.9, -27.98) * mm});
            skLineSegment(sketch, "E5.67.0", {"start": v(-29.9, -29.05) * mm, "end": v(-30.58, -29.71) * mm});
            skLineSegment(sketch, "E5.67.1", {"start": v(-30.76, -29.53) * mm, "end": v(-30.07, -28.86) * mm});
            skLineSegment(sketch, "E5.67.2", {"start": v(-30.58, -29.71) * mm, "end": v(-30.76, -29.53) * mm});
            skArc(sketch, "E5.67.3", {"start": v(-30.07, -28.86) * mm, "mid": v(-29.98, -28.95) * mm, "end": v(-29.9, -29.05) * mm});
            skLineSegment(sketch, "E5.68.0", {"start": v(-28.86, -30.07) * mm, "end": v(-29.53, -30.76) * mm});
            skLineSegment(sketch, "E5.68.1", {"start": v(-29.71, -30.58) * mm, "end": v(-29.05, -29.9) * mm});
            skLineSegment(sketch, "E5.68.2", {"start": v(-29.53, -30.76) * mm, "end": v(-29.71, -30.58) * mm});
            skArc(sketch, "E5.68.3", {"start": v(-29.05, -29.9) * mm, "mid": v(-28.95, -29.98) * mm, "end": v(-28.86, -30.07) * mm});
            skLineSegment(sketch, "E5.69.0", {"start": v(-27.8, -31.06) * mm, "end": v(-28.44, -31.77) * mm});
            skLineSegment(sketch, "E5.69.1", {"start": v(-28.63, -31.6) * mm, "end": v(-27.98, -30.9) * mm});
            skLineSegment(sketch, "E5.69.2", {"start": v(-28.44, -31.77) * mm, "end": v(-28.63, -31.6) * mm});
            skArc(sketch, "E5.69.3", {"start": v(-27.98, -30.9) * mm, "mid": v(-27.9, -30.98) * mm, "end": v(-27.8, -31.06) * mm});
            skLineSegment(sketch, "E5.70.0", {"start": v(-26.7, -32.01) * mm, "end": v(-27.31, -32.74) * mm});
            skLineSegment(sketch, "E5.70.1", {"start": v(-27.5, -32.58) * mm, "end": v(-26.89, -31.85) * mm});
            skLineSegment(sketch, "E5.70.2", {"start": v(-27.31, -32.74) * mm, "end": v(-27.5, -32.58) * mm});
            skArc(sketch, "E5.70.3", {"start": v(-26.89, -31.85) * mm, "mid": v(-26.8, -31.93) * mm, "end": v(-26.7, -32.01) * mm});
            skLineSegment(sketch, "E5.71.0", {"start": v(-25.56, -32.92) * mm, "end": v(-26.15, -33.68) * mm});
            skLineSegment(sketch, "E5.71.1", {"start": v(-26.35, -33.52) * mm, "end": v(-25.76, -32.77) * mm});
            skLineSegment(sketch, "E5.71.2", {"start": v(-26.15, -33.68) * mm, "end": v(-26.35, -33.52) * mm});
            skArc(sketch, "E5.71.3", {"start": v(-25.76, -32.77) * mm, "mid": v(-25.66, -32.85) * mm, "end": v(-25.56, -32.92) * mm});
            skLineSegment(sketch, "E5.72.0", {"start": v(-24.4, -33.8) * mm, "end": v(-24.96, -34.57) * mm});
            skLineSegment(sketch, "E5.72.1", {"start": v(-25.17, -34.42) * mm, "end": v(-24.6, -33.65) * mm});
            skLineSegment(sketch, "E5.72.2", {"start": v(-24.96, -34.57) * mm, "end": v(-25.17, -34.42) * mm});
            skArc(sketch, "E5.72.3", {"start": v(-24.6, -33.65) * mm, "mid": v(-24.5, -33.72) * mm, "end": v(-24.4, -33.8) * mm});
            skLineSegment(sketch, "E5.73.0", {"start": v(-23.2, -34.63) * mm, "end": v(-23.74, -35.42) * mm});
            skLineSegment(sketch, "E5.73.1", {"start": v(-23.95, -35.28) * mm, "end": v(-23.41, -34.48) * mm});
            skLineSegment(sketch, "E5.73.2", {"start": v(-23.74, -35.42) * mm, "end": v(-23.95, -35.28) * mm});
            skArc(sketch, "E5.73.3", {"start": v(-23.41, -34.48) * mm, "mid": v(-23.3, -34.56) * mm, "end": v(-23.2, -34.63) * mm});
            skLineSegment(sketch, "E5.74.0", {"start": v(-21.98, -35.41) * mm, "end": v(-22.49, -36.23) * mm});
            skLineSegment(sketch, "E5.74.1", {"start": v(-22.7, -36.1) * mm, "end": v(-22.2, -35.28) * mm});
            skLineSegment(sketch, "E5.74.2", {"start": v(-22.49, -36.23) * mm, "end": v(-22.7, -36.1) * mm});
            skArc(sketch, "E5.74.3", {"start": v(-22.2, -35.28) * mm, "mid": v(-22.09, -35.35) * mm, "end": v(-21.98, -35.41) * mm});
            skLineSegment(sketch, "E5.75.0", {"start": v(-20.73, -36.16) * mm, "end": v(-21.2, -36.99) * mm});
            skLineSegment(sketch, "E5.75.1", {"start": v(-21.43, -36.86) * mm, "end": v(-20.95, -36.03) * mm});
            skLineSegment(sketch, "E5.75.2", {"start": v(-21.2, -36.99) * mm, "end": v(-21.43, -36.86) * mm});
            skArc(sketch, "E5.75.3", {"start": v(-20.95, -36.03) * mm, "mid": v(-20.84, -36.1) * mm, "end": v(-20.73, -36.16) * mm});
            skLineSegment(sketch, "E5.76.0", {"start": v(-19.46, -36.86) * mm, "end": v(-19.9, -37.7) * mm});
            skLineSegment(sketch, "E5.76.1", {"start": v(-20.13, -37.59) * mm, "end": v(-19.68, -36.74) * mm});
            skLineSegment(sketch, "E5.76.2", {"start": v(-19.9, -37.7) * mm, "end": v(-20.13, -37.59) * mm});
            skArc(sketch, "E5.76.3", {"start": v(-19.68, -36.74) * mm, "mid": v(-19.57, -36.8) * mm, "end": v(-19.46, -36.86) * mm});
            skLineSegment(sketch, "E5.77.0", {"start": v(-18.16, -37.52) * mm, "end": v(-18.58, -38.38) * mm});
            skLineSegment(sketch, "E5.77.1", {"start": v(-18.8, -38.27) * mm, "end": v(-18.39, -37.4) * mm});
            skLineSegment(sketch, "E5.77.2", {"start": v(-18.58, -38.38) * mm, "end": v(-18.8, -38.27) * mm});
            skArc(sketch, "E5.77.3", {"start": v(-18.39, -37.4) * mm, "mid": v(-18.27, -37.46) * mm, "end": v(-18.16, -37.52) * mm});
            skLineSegment(sketch, "E5.78.0", {"start": v(-16.84, -38.13) * mm, "end": v(-17.23, -39) * mm});
            skLineSegment(sketch, "E5.78.1", {"start": v(-17.46, -38.9) * mm, "end": v(-17.07, -38.03) * mm});
            skLineSegment(sketch, "E5.78.2", {"start": v(-17.23, -39) * mm, "end": v(-17.46, -38.9) * mm});
            skArc(sketch, "E5.78.3", {"start": v(-17.07, -38.03) * mm, "mid": v(-16.95, -38.08) * mm, "end": v(-16.84, -38.13) * mm});
            skLineSegment(sketch, "E5.79.0", {"start": v(-15.5, -38.7) * mm, "end": v(-15.86, -39.58) * mm});
            skLineSegment(sketch, "E5.79.1", {"start": v(-16.1, -39.49) * mm, "end": v(-15.73, -38.6) * mm});
            skLineSegment(sketch, "E5.79.2", {"start": v(-15.86, -39.58) * mm, "end": v(-16.1, -39.49) * mm});
            skArc(sketch, "E5.79.3", {"start": v(-15.73, -38.6) * mm, "mid": v(-15.61, -38.65) * mm, "end": v(-15.5, -38.7) * mm});
            skLineSegment(sketch, "E5.80.0", {"start": v(-14.14, -39.21) * mm, "end": v(-14.46, -40.11) * mm});
            skLineSegment(sketch, "E5.80.1", {"start": v(-14.7, -40.02) * mm, "end": v(-14.38, -39.12) * mm});
            skLineSegment(sketch, "E5.80.2", {"start": v(-14.46, -40.11) * mm, "end": v(-14.7, -40.02) * mm});
            skArc(sketch, "E5.80.3", {"start": v(-14.38, -39.12) * mm, "mid": v(-14.26, -39.17) * mm, "end": v(-14.14, -39.21) * mm});
            skLineSegment(sketch, "E5.81.0", {"start": v(-12.76, -39.68) * mm, "end": v(-13.06, -40.6) * mm});
            skLineSegment(sketch, "E5.81.1", {"start": v(-13.3, -40.51) * mm, "end": v(-13, -39.6) * mm});
            skLineSegment(sketch, "E5.81.2", {"start": v(-13.06, -40.6) * mm, "end": v(-13.3, -40.51) * mm});
            skArc(sketch, "E5.81.3", {"start": v(-13, -39.6) * mm, "mid": v(-12.88, -39.64) * mm, "end": v(-12.76, -39.68) * mm});
            skLineSegment(sketch, "E5.82.0", {"start": v(-11.37, -40.1) * mm, "end": v(-11.63, -41.02) * mm});
            skLineSegment(sketch, "E5.82.1", {"start": v(-11.87, -40.95) * mm, "end": v(-11.61, -40.03) * mm});
            skLineSegment(sketch, "E5.82.2", {"start": v(-11.63, -41.02) * mm, "end": v(-11.87, -40.95) * mm});
            skArc(sketch, "E5.82.3", {"start": v(-11.61, -40.03) * mm, "mid": v(-11.49, -40.07) * mm, "end": v(-11.37, -40.1) * mm});
            skLineSegment(sketch, "E5.83.0", {"start": v(-9.96, -40.47) * mm, "end": v(-10.2, -41.4) * mm});
            skLineSegment(sketch, "E5.83.1", {"start": v(-10.44, -41.34) * mm, "end": v(-10.2, -40.41) * mm});
            skLineSegment(sketch, "E5.83.2", {"start": v(-10.2, -41.4) * mm, "end": v(-10.44, -41.34) * mm});
            skArc(sketch, "E5.83.3", {"start": v(-10.2, -40.41) * mm, "mid": v(-10.08, -40.44) * mm, "end": v(-9.96, -40.47) * mm});
            skLineSegment(sketch, "E5.84.0", {"start": v(-8.54, -40.8) * mm, "end": v(-8.74, -41.73) * mm});
            skLineSegment(sketch, "E5.84.1", {"start": v(-8.99, -41.68) * mm, "end": v(-8.8, -40.74) * mm});
            skLineSegment(sketch, "E5.84.2", {"start": v(-8.74, -41.73) * mm, "end": v(-8.99, -41.68) * mm});
            skArc(sketch, "E5.84.3", {"start": v(-8.8, -40.74) * mm, "mid": v(-8.67, -40.77) * mm, "end": v(-8.54, -40.8) * mm});
            skLineSegment(sketch, "E5.85.0", {"start": v(-7.11, -41.07) * mm, "end": v(-7.28, -42.01) * mm});
            skLineSegment(sketch, "E5.85.1", {"start": v(-7.53, -41.97) * mm, "end": v(-7.36, -41.03) * mm});
            skLineSegment(sketch, "E5.85.2", {"start": v(-7.28, -42.01) * mm, "end": v(-7.53, -41.97) * mm});
            skArc(sketch, "E5.85.3", {"start": v(-7.36, -41.03) * mm, "mid": v(-7.24, -41.05) * mm, "end": v(-7.11, -41.07) * mm});
            skLineSegment(sketch, "E5.86.0", {"start": v(-5.68, -41.3) * mm, "end": v(-5.8, -42.24) * mm});
            skLineSegment(sketch, "E5.86.1", {"start": v(-6.06, -42.2) * mm, "end": v(-5.93, -41.26) * mm});
            skLineSegment(sketch, "E5.86.2", {"start": v(-5.8, -42.24) * mm, "end": v(-6.06, -42.2) * mm});
            skArc(sketch, "E5.86.3", {"start": v(-5.93, -41.26) * mm, "mid": v(-5.8, -41.28) * mm, "end": v(-5.68, -41.3) * mm});
            skLineSegment(sketch, "E5.87.0", {"start": v(-4.23, -41.47) * mm, "end": v(-4.33, -42.42) * mm});
            skLineSegment(sketch, "E5.87.1", {"start": v(-4.58, -42.4) * mm, "end": v(-4.48, -41.44) * mm});
            skLineSegment(sketch, "E5.87.2", {"start": v(-4.33, -42.42) * mm, "end": v(-4.58, -42.4) * mm});
            skArc(sketch, "E5.87.3", {"start": v(-4.48, -41.44) * mm, "mid": v(-4.36, -41.45) * mm, "end": v(-4.23, -41.47) * mm});
            skLineSegment(sketch, "E5.88.0", {"start": v(-2.78, -41.59) * mm, "end": v(-2.85, -42.54) * mm});
            skLineSegment(sketch, "E5.88.1", {"start": v(-3.1, -42.53) * mm, "end": v(-3.03, -41.57) * mm});
            skLineSegment(sketch, "E5.88.2", {"start": v(-2.85, -42.54) * mm, "end": v(-3.1, -42.53) * mm});
            skArc(sketch, "E5.88.3", {"start": v(-3.03, -41.57) * mm, "mid": v(-2.9, -41.58) * mm, "end": v(-2.78, -41.59) * mm});
            skLineSegment(sketch, "E5.89.0", {"start": v(-1.33, -41.66) * mm, "end": v(-1.36, -42.62) * mm});
            skLineSegment(sketch, "E5.89.1", {"start": v(-1.62, -42.6) * mm, "end": v(-1.58, -41.65) * mm});
            skLineSegment(sketch, "E5.89.2", {"start": v(-1.36, -42.62) * mm, "end": v(-1.62, -42.6) * mm});
            skArc(sketch, "E5.89.3", {"start": v(-1.58, -41.65) * mm, "mid": v(-1.45, -41.66) * mm, "end": v(-1.33, -41.66) * mm});
            skLineSegment(sketch, "E5.90.0", {"start": v(0.13, -41.68) * mm, "end": v(0.13, -42.64) * mm});
            skLineSegment(sketch, "E5.90.1", {"start": v(-0.13, -42.64) * mm, "end": v(-0.13, -41.68) * mm});
            skLineSegment(sketch, "E5.90.2", {"start": v(0.13, -42.64) * mm, "end": v(-0.13, -42.64) * mm});
            skArc(sketch, "E5.90.3", {"start": v(-0.13, -41.68) * mm, "mid": v(0, -41.68) * mm, "end": v(0.13, -41.68) * mm});
            skLineSegment(sketch, "E5.91.0", {"start": v(1.58, -41.65) * mm, "end": v(1.62, -42.6) * mm});
            skLineSegment(sketch, "E5.91.1", {"start": v(1.36, -42.62) * mm, "end": v(1.33, -41.66) * mm});
            skLineSegment(sketch, "E5.91.2", {"start": v(1.62, -42.6) * mm, "end": v(1.36, -42.62) * mm});
            skArc(sketch, "E5.91.3", {"start": v(1.33, -41.66) * mm, "mid": v(1.45, -41.66) * mm, "end": v(1.58, -41.65) * mm});
            skLineSegment(sketch, "E5.92.0", {"start": v(3.03, -41.57) * mm, "end": v(3.1, -42.53) * mm});
            skLineSegment(sketch, "E5.92.1", {"start": v(2.85, -42.54) * mm, "end": v(2.78, -41.59) * mm});
            skLineSegment(sketch, "E5.92.2", {"start": v(3.1, -42.53) * mm, "end": v(2.85, -42.54) * mm});
            skArc(sketch, "E5.92.3", {"start": v(2.78, -41.59) * mm, "mid": v(2.9, -41.58) * mm, "end": v(3.03, -41.57) * mm});
            skLineSegment(sketch, "E5.93.0", {"start": v(4.48, -41.44) * mm, "end": v(4.58, -42.4) * mm});
            skLineSegment(sketch, "E5.93.1", {"start": v(4.33, -42.42) * mm, "end": v(4.23, -41.47) * mm});
            skLineSegment(sketch, "E5.93.2", {"start": v(4.58, -42.4) * mm, "end": v(4.33, -42.42) * mm});
            skArc(sketch, "E5.93.3", {"start": v(4.23, -41.47) * mm, "mid": v(4.36, -41.45) * mm, "end": v(4.48, -41.44) * mm});
            skLineSegment(sketch, "E5.94.0", {"start": v(5.93, -41.26) * mm, "end": v(6.06, -42.2) * mm});
            skLineSegment(sketch, "E5.94.1", {"start": v(5.8, -42.24) * mm, "end": v(5.68, -41.3) * mm});
            skLineSegment(sketch, "E5.94.2", {"start": v(6.06, -42.2) * mm, "end": v(5.8, -42.24) * mm});
            skArc(sketch, "E5.94.3", {"start": v(5.68, -41.3) * mm, "mid": v(5.8, -41.28) * mm, "end": v(5.93, -41.26) * mm});
            skLineSegment(sketch, "E5.95.0", {"start": v(7.36, -41.03) * mm, "end": v(7.53, -41.97) * mm});
            skLineSegment(sketch, "E5.95.1", {"start": v(7.28, -42.01) * mm, "end": v(7.11, -41.07) * mm});
            skLineSegment(sketch, "E5.95.2", {"start": v(7.53, -41.97) * mm, "end": v(7.28, -42.01) * mm});
            skArc(sketch, "E5.95.3", {"start": v(7.11, -41.07) * mm, "mid": v(7.24, -41.05) * mm, "end": v(7.36, -41.03) * mm});
            skLineSegment(sketch, "E5.96.0", {"start": v(8.8, -40.74) * mm, "end": v(8.99, -41.68) * mm});
            skLineSegment(sketch, "E5.96.1", {"start": v(8.74, -41.73) * mm, "end": v(8.54, -40.8) * mm});
            skLineSegment(sketch, "E5.96.2", {"start": v(8.99, -41.68) * mm, "end": v(8.74, -41.73) * mm});
            skArc(sketch, "E5.96.3", {"start": v(8.54, -40.8) * mm, "mid": v(8.67, -40.77) * mm, "end": v(8.8, -40.74) * mm});
            skLineSegment(sketch, "E5.97.0", {"start": v(10.2, -40.41) * mm, "end": v(10.44, -41.34) * mm});
            skLineSegment(sketch, "E5.97.1", {"start": v(10.2, -41.4) * mm, "end": v(9.96, -40.47) * mm});
            skLineSegment(sketch, "E5.97.2", {"start": v(10.44, -41.34) * mm, "end": v(10.2, -41.4) * mm});
            skArc(sketch, "E5.97.3", {"start": v(9.96, -40.47) * mm, "mid": v(10.08, -40.44) * mm, "end": v(10.2, -40.41) * mm});
            skLineSegment(sketch, "E5.98.0", {"start": v(11.61, -40.03) * mm, "end": v(11.87, -40.95) * mm});
            skLineSegment(sketch, "E5.98.1", {"start": v(11.63, -41.02) * mm, "end": v(11.37, -40.1) * mm});
            skLineSegment(sketch, "E5.98.2", {"start": v(11.87, -40.95) * mm, "end": v(11.63, -41.02) * mm});
            skArc(sketch, "E5.98.3", {"start": v(11.37, -40.1) * mm, "mid": v(11.49, -40.07) * mm, "end": v(11.61, -40.03) * mm});
            skLineSegment(sketch, "E5.99.0", {"start": v(13, -39.6) * mm, "end": v(13.3, -40.51) * mm});
            skLineSegment(sketch, "E5.99.1", {"start": v(13.06, -40.6) * mm, "end": v(12.76, -39.68) * mm});
            skLineSegment(sketch, "E5.99.2", {"start": v(13.3, -40.51) * mm, "end": v(13.06, -40.6) * mm});
            skArc(sketch, "E5.99.3", {"start": v(12.76, -39.68) * mm, "mid": v(12.88, -39.64) * mm, "end": v(13, -39.6) * mm});
            skLineSegment(sketch, "E5.100.0", {"start": v(14.38, -39.12) * mm, "end": v(14.7, -40.02) * mm});
            skLineSegment(sketch, "E5.100.1", {"start": v(14.46, -40.11) * mm, "end": v(14.14, -39.21) * mm});
            skLineSegment(sketch, "E5.100.2", {"start": v(14.7, -40.02) * mm, "end": v(14.46, -40.11) * mm});
            skArc(sketch, "E5.100.3", {"start": v(14.14, -39.21) * mm, "mid": v(14.26, -39.17) * mm, "end": v(14.38, -39.12) * mm});
            skLineSegment(sketch, "E5.101.0", {"start": v(15.73, -38.6) * mm, "end": v(16.1, -39.49) * mm});
            skLineSegment(sketch, "E5.101.1", {"start": v(15.86, -39.58) * mm, "end": v(15.5, -38.7) * mm});
            skLineSegment(sketch, "E5.101.2", {"start": v(16.1, -39.49) * mm, "end": v(15.86, -39.58) * mm});
            skArc(sketch, "E5.101.3", {"start": v(15.5, -38.7) * mm, "mid": v(15.61, -38.65) * mm, "end": v(15.73, -38.6) * mm});
            skLineSegment(sketch, "E5.102.0", {"start": v(17.07, -38.03) * mm, "end": v(17.46, -38.9) * mm});
            skLineSegment(sketch, "E5.102.1", {"start": v(17.23, -39) * mm, "end": v(16.84, -38.13) * mm});
            skLineSegment(sketch, "E5.102.2", {"start": v(17.46, -38.9) * mm, "end": v(17.23, -39) * mm});
            skArc(sketch, "E5.102.3", {"start": v(16.84, -38.13) * mm, "mid": v(16.95, -38.08) * mm, "end": v(17.07, -38.03) * mm});
            skLineSegment(sketch, "E5.103.0", {"start": v(18.39, -37.4) * mm, "end": v(18.8, -38.27) * mm});
            skLineSegment(sketch, "E5.103.1", {"start": v(18.58, -38.38) * mm, "end": v(18.16, -37.52) * mm});
            skLineSegment(sketch, "E5.103.2", {"start": v(18.8, -38.27) * mm, "end": v(18.58, -38.38) * mm});
            skArc(sketch, "E5.103.3", {"start": v(18.16, -37.52) * mm, "mid": v(18.27, -37.46) * mm, "end": v(18.39, -37.4) * mm});
            skLineSegment(sketch, "E5.104.0", {"start": v(19.68, -36.74) * mm, "end": v(20.13, -37.59) * mm});
            skLineSegment(sketch, "E5.104.1", {"start": v(19.9, -37.7) * mm, "end": v(19.46, -36.86) * mm});
            skLineSegment(sketch, "E5.104.2", {"start": v(20.13, -37.59) * mm, "end": v(19.9, -37.7) * mm});
            skArc(sketch, "E5.104.3", {"start": v(19.46, -36.86) * mm, "mid": v(19.57, -36.8) * mm, "end": v(19.68, -36.74) * mm});
            skLineSegment(sketch, "E5.105.0", {"start": v(20.95, -36.03) * mm, "end": v(21.43, -36.86) * mm});
            skLineSegment(sketch, "E5.105.1", {"start": v(21.2, -36.99) * mm, "end": v(20.73, -36.16) * mm});
            skLineSegment(sketch, "E5.105.2", {"start": v(21.43, -36.86) * mm, "end": v(21.2, -36.99) * mm});
            skArc(sketch, "E5.105.3", {"start": v(20.73, -36.16) * mm, "mid": v(20.84, -36.1) * mm, "end": v(20.95, -36.03) * mm});
            skLineSegment(sketch, "E5.106.0", {"start": v(22.2, -35.28) * mm, "end": v(22.7, -36.1) * mm});
            skLineSegment(sketch, "E5.106.1", {"start": v(22.49, -36.23) * mm, "end": v(21.98, -35.41) * mm});
            skLineSegment(sketch, "E5.106.2", {"start": v(22.7, -36.1) * mm, "end": v(22.49, -36.23) * mm});
            skArc(sketch, "E5.106.3", {"start": v(21.98, -35.41) * mm, "mid": v(22.09, -35.35) * mm, "end": v(22.2, -35.28) * mm});
            skLineSegment(sketch, "E5.107.0", {"start": v(23.41, -34.48) * mm, "end": v(23.95, -35.28) * mm});
            skLineSegment(sketch, "E5.107.1", {"start": v(23.74, -35.42) * mm, "end": v(23.2, -34.63) * mm});
            skLineSegment(sketch, "E5.107.2", {"start": v(23.95, -35.28) * mm, "end": v(23.74, -35.42) * mm});
            skArc(sketch, "E5.107.3", {"start": v(23.2, -34.63) * mm, "mid": v(23.3, -34.56) * mm, "end": v(23.41, -34.48) * mm});
            skLineSegment(sketch, "E5.108.0", {"start": v(24.6, -33.65) * mm, "end": v(25.17, -34.42) * mm});
            skLineSegment(sketch, "E5.108.1", {"start": v(24.96, -34.57) * mm, "end": v(24.4, -33.8) * mm});
            skLineSegment(sketch, "E5.108.2", {"start": v(25.17, -34.42) * mm, "end": v(24.96, -34.57) * mm});
            skArc(sketch, "E5.108.3", {"start": v(24.4, -33.8) * mm, "mid": v(24.5, -33.72) * mm, "end": v(24.6, -33.65) * mm});
            skLineSegment(sketch, "E5.109.0", {"start": v(25.76, -32.77) * mm, "end": v(26.35, -33.52) * mm});
            skLineSegment(sketch, "E5.109.1", {"start": v(26.15, -33.68) * mm, "end": v(25.56, -32.92) * mm});
            skLineSegment(sketch, "E5.109.2", {"start": v(26.35, -33.52) * mm, "end": v(26.15, -33.68) * mm});
            skArc(sketch, "E5.109.3", {"start": v(25.56, -32.92) * mm, "mid": v(25.66, -32.85) * mm, "end": v(25.76, -32.77) * mm});
            skLineSegment(sketch, "E5.110.0", {"start": v(26.89, -31.85) * mm, "end": v(27.5, -32.58) * mm});
            skLineSegment(sketch, "E5.110.1", {"start": v(27.31, -32.74) * mm, "end": v(26.7, -32.01) * mm});
            skLineSegment(sketch, "E5.110.2", {"start": v(27.5, -32.58) * mm, "end": v(27.31, -32.74) * mm});
            skArc(sketch, "E5.110.3", {"start": v(26.7, -32.01) * mm, "mid": v(26.8, -31.93) * mm, "end": v(26.89, -31.85) * mm});
            skLineSegment(sketch, "E5.111.0", {"start": v(27.98, -30.9) * mm, "end": v(28.63, -31.6) * mm});
            skLineSegment(sketch, "E5.111.1", {"start": v(28.44, -31.77) * mm, "end": v(27.8, -31.06) * mm});
            skLineSegment(sketch, "E5.111.2", {"start": v(28.63, -31.6) * mm, "end": v(28.44, -31.77) * mm});
            skArc(sketch, "E5.111.3", {"start": v(27.8, -31.06) * mm, "mid": v(27.9, -30.98) * mm, "end": v(27.98, -30.9) * mm});
            skLineSegment(sketch, "E5.112.0", {"start": v(29.05, -29.9) * mm, "end": v(29.71, -30.58) * mm});
            skLineSegment(sketch, "E5.112.1", {"start": v(29.53, -30.76) * mm, "end": v(28.86, -30.07) * mm});
            skLineSegment(sketch, "E5.112.2", {"start": v(29.71, -30.58) * mm, "end": v(29.53, -30.76) * mm});
            skArc(sketch, "E5.112.3", {"start": v(28.86, -30.07) * mm, "mid": v(28.95, -29.98) * mm, "end": v(29.05, -29.9) * mm});
            skLineSegment(sketch, "E5.113.0", {"start": v(30.07, -28.86) * mm, "end": v(30.76, -29.53) * mm});
            skLineSegment(sketch, "E5.113.1", {"start": v(30.58, -29.71) * mm, "end": v(29.9, -29.05) * mm});
            skLineSegment(sketch, "E5.113.2", {"start": v(30.76, -29.53) * mm, "end": v(30.58, -29.71) * mm});
            skArc(sketch, "E5.113.3", {"start": v(29.9, -29.05) * mm, "mid": v(29.98, -28.95) * mm, "end": v(30.07, -28.86) * mm});
            skLineSegment(sketch, "E5.114.0", {"start": v(31.06, -27.8) * mm, "end": v(31.77, -28.44) * mm});
            skLineSegment(sketch, "E5.114.1", {"start": v(31.6, -28.63) * mm, "end": v(30.9, -27.98) * mm});
            skLineSegment(sketch, "E5.114.2", {"start": v(31.77, -28.44) * mm, "end": v(31.6, -28.63) * mm});
            skArc(sketch, "E5.114.3", {"start": v(30.9, -27.98) * mm, "mid": v(30.98, -27.9) * mm, "end": v(31.06, -27.8) * mm});
            skLineSegment(sketch, "E5.115.0", {"start": v(32.01, -26.7) * mm, "end": v(32.74, -27.31) * mm});
            skLineSegment(sketch, "E5.115.1", {"start": v(32.58, -27.5) * mm, "end": v(31.85, -26.89) * mm});
            skLineSegment(sketch, "E5.115.2", {"start": v(32.74, -27.31) * mm, "end": v(32.58, -27.5) * mm});
            skArc(sketch, "E5.115.3", {"start": v(31.85, -26.89) * mm, "mid": v(31.93, -26.8) * mm, "end": v(32.01, -26.7) * mm});
            skLineSegment(sketch, "E5.116.0", {"start": v(32.92, -25.56) * mm, "end": v(33.68, -26.15) * mm});
            skLineSegment(sketch, "E5.116.1", {"start": v(33.52, -26.35) * mm, "end": v(32.77, -25.76) * mm});
            skLineSegment(sketch, "E5.116.2", {"start": v(33.68, -26.15) * mm, "end": v(33.52, -26.35) * mm});
            skArc(sketch, "E5.116.3", {"start": v(32.77, -25.76) * mm, "mid": v(32.85, -25.66) * mm, "end": v(32.92, -25.56) * mm});
            skLineSegment(sketch, "E5.117.0", {"start": v(33.8, -24.4) * mm, "end": v(34.57, -24.96) * mm});
            skLineSegment(sketch, "E5.117.1", {"start": v(34.42, -25.17) * mm, "end": v(33.65, -24.6) * mm});
            skLineSegment(sketch, "E5.117.2", {"start": v(34.57, -24.96) * mm, "end": v(34.42, -25.17) * mm});
            skArc(sketch, "E5.117.3", {"start": v(33.65, -24.6) * mm, "mid": v(33.72, -24.5) * mm, "end": v(33.8, -24.4) * mm});
            skLineSegment(sketch, "E5.118.0", {"start": v(34.63, -23.2) * mm, "end": v(35.42, -23.74) * mm});
            skLineSegment(sketch, "E5.118.1", {"start": v(35.28, -23.95) * mm, "end": v(34.48, -23.41) * mm});
            skLineSegment(sketch, "E5.118.2", {"start": v(35.42, -23.74) * mm, "end": v(35.28, -23.95) * mm});
            skArc(sketch, "E5.118.3", {"start": v(34.48, -23.41) * mm, "mid": v(34.56, -23.3) * mm, "end": v(34.63, -23.2) * mm});
            skLineSegment(sketch, "E5.119.0", {"start": v(35.41, -21.98) * mm, "end": v(36.23, -22.49) * mm});
            skLineSegment(sketch, "E5.119.1", {"start": v(36.1, -22.7) * mm, "end": v(35.28, -22.2) * mm});
            skLineSegment(sketch, "E5.119.2", {"start": v(36.23, -22.49) * mm, "end": v(36.1, -22.7) * mm});
            skArc(sketch, "E5.119.3", {"start": v(35.28, -22.2) * mm, "mid": v(35.35, -22.09) * mm, "end": v(35.41, -21.98) * mm});
            skLineSegment(sketch, "E5.120.0", {"start": v(36.16, -20.73) * mm, "end": v(36.99, -21.2) * mm});
            skLineSegment(sketch, "E5.120.1", {"start": v(36.86, -21.43) * mm, "end": v(36.03, -20.95) * mm});
            skLineSegment(sketch, "E5.120.2", {"start": v(36.99, -21.2) * mm, "end": v(36.86, -21.43) * mm});
            skArc(sketch, "E5.120.3", {"start": v(36.03, -20.95) * mm, "mid": v(36.1, -20.84) * mm, "end": v(36.16, -20.73) * mm});
            skLineSegment(sketch, "E5.121.0", {"start": v(36.86, -19.46) * mm, "end": v(37.7, -19.9) * mm});
            skLineSegment(sketch, "E5.121.1", {"start": v(37.59, -20.13) * mm, "end": v(36.74, -19.68) * mm});
            skLineSegment(sketch, "E5.121.2", {"start": v(37.7, -19.9) * mm, "end": v(37.59, -20.13) * mm});
            skArc(sketch, "E5.121.3", {"start": v(36.74, -19.68) * mm, "mid": v(36.8, -19.57) * mm, "end": v(36.86, -19.46) * mm});
            skLineSegment(sketch, "E5.122.0", {"start": v(37.52, -18.16) * mm, "end": v(38.38, -18.58) * mm});
            skLineSegment(sketch, "E5.122.1", {"start": v(38.27, -18.8) * mm, "end": v(37.4, -18.39) * mm});
            skLineSegment(sketch, "E5.122.2", {"start": v(38.38, -18.58) * mm, "end": v(38.27, -18.8) * mm});
            skArc(sketch, "E5.122.3", {"start": v(37.4, -18.39) * mm, "mid": v(37.46, -18.27) * mm, "end": v(37.52, -18.16) * mm});
            skLineSegment(sketch, "E5.123.0", {"start": v(38.13, -16.84) * mm, "end": v(39, -17.23) * mm});
            skLineSegment(sketch, "E5.123.1", {"start": v(38.9, -17.46) * mm, "end": v(38.03, -17.07) * mm});
            skLineSegment(sketch, "E5.123.2", {"start": v(39, -17.23) * mm, "end": v(38.9, -17.46) * mm});
            skArc(sketch, "E5.123.3", {"start": v(38.03, -17.07) * mm, "mid": v(38.08, -16.95) * mm, "end": v(38.13, -16.84) * mm});
            skLineSegment(sketch, "E5.124.0", {"start": v(38.7, -15.5) * mm, "end": v(39.58, -15.86) * mm});
            skLineSegment(sketch, "E5.124.1", {"start": v(39.49, -16.1) * mm, "end": v(38.6, -15.73) * mm});
            skLineSegment(sketch, "E5.124.2", {"start": v(39.58, -15.86) * mm, "end": v(39.49, -16.1) * mm});
            skArc(sketch, "E5.124.3", {"start": v(38.6, -15.73) * mm, "mid": v(38.65, -15.61) * mm, "end": v(38.7, -15.5) * mm});
            skLineSegment(sketch, "E5.125.0", {"start": v(39.21, -14.14) * mm, "end": v(40.11, -14.46) * mm});
            skLineSegment(sketch, "E5.125.1", {"start": v(40.02, -14.7) * mm, "end": v(39.12, -14.38) * mm});
            skLineSegment(sketch, "E5.125.2", {"start": v(40.11, -14.46) * mm, "end": v(40.02, -14.7) * mm});
            skArc(sketch, "E5.125.3", {"start": v(39.12, -14.38) * mm, "mid": v(39.17, -14.26) * mm, "end": v(39.21, -14.14) * mm});
            skLineSegment(sketch, "E5.126.0", {"start": v(39.68, -12.76) * mm, "end": v(40.6, -13.06) * mm});
            skLineSegment(sketch, "E5.126.1", {"start": v(40.51, -13.3) * mm, "end": v(39.6, -13) * mm});
            skLineSegment(sketch, "E5.126.2", {"start": v(40.6, -13.06) * mm, "end": v(40.51, -13.3) * mm});
            skArc(sketch, "E5.126.3", {"start": v(39.6, -13) * mm, "mid": v(39.64, -12.88) * mm, "end": v(39.68, -12.76) * mm});
            skLineSegment(sketch, "E5.127.0", {"start": v(40.1, -11.37) * mm, "end": v(41.02, -11.63) * mm});
            skLineSegment(sketch, "E5.127.1", {"start": v(40.95, -11.87) * mm, "end": v(40.03, -11.61) * mm});
            skLineSegment(sketch, "E5.127.2", {"start": v(41.02, -11.63) * mm, "end": v(40.95, -11.87) * mm});
            skArc(sketch, "E5.127.3", {"start": v(40.03, -11.61) * mm, "mid": v(40.07, -11.49) * mm, "end": v(40.1, -11.37) * mm});
            skLineSegment(sketch, "E5.128.0", {"start": v(40.47, -9.96) * mm, "end": v(41.4, -10.2) * mm});
            skLineSegment(sketch, "E5.128.1", {"start": v(41.34, -10.44) * mm, "end": v(40.41, -10.2) * mm});
            skLineSegment(sketch, "E5.128.2", {"start": v(41.4, -10.2) * mm, "end": v(41.34, -10.44) * mm});
            skArc(sketch, "E5.128.3", {"start": v(40.41, -10.2) * mm, "mid": v(40.44, -10.08) * mm, "end": v(40.47, -9.96) * mm});
            skLineSegment(sketch, "E5.129.0", {"start": v(40.8, -8.54) * mm, "end": v(41.73, -8.74) * mm});
            skLineSegment(sketch, "E5.129.1", {"start": v(41.68, -8.99) * mm, "end": v(40.74, -8.8) * mm});
            skLineSegment(sketch, "E5.129.2", {"start": v(41.73, -8.74) * mm, "end": v(41.68, -8.99) * mm});
            skArc(sketch, "E5.129.3", {"start": v(40.74, -8.8) * mm, "mid": v(40.77, -8.67) * mm, "end": v(40.8, -8.54) * mm});
            skLineSegment(sketch, "E5.130.0", {"start": v(41.07, -7.11) * mm, "end": v(42.01, -7.28) * mm});
            skLineSegment(sketch, "E5.130.1", {"start": v(41.97, -7.53) * mm, "end": v(41.03, -7.36) * mm});
            skLineSegment(sketch, "E5.130.2", {"start": v(42.01, -7.28) * mm, "end": v(41.97, -7.53) * mm});
            skArc(sketch, "E5.130.3", {"start": v(41.03, -7.36) * mm, "mid": v(41.05, -7.24) * mm, "end": v(41.07, -7.11) * mm});
            skLineSegment(sketch, "E5.131.0", {"start": v(41.3, -5.68) * mm, "end": v(42.24, -5.8) * mm});
            skLineSegment(sketch, "E5.131.1", {"start": v(42.2, -6.06) * mm, "end": v(41.26, -5.93) * mm});
            skLineSegment(sketch, "E5.131.2", {"start": v(42.24, -5.8) * mm, "end": v(42.2, -6.06) * mm});
            skArc(sketch, "E5.131.3", {"start": v(41.26, -5.93) * mm, "mid": v(41.28, -5.8) * mm, "end": v(41.3, -5.68) * mm});
            skLineSegment(sketch, "E5.132.0", {"start": v(41.47, -4.23) * mm, "end": v(42.42, -4.33) * mm});
            skLineSegment(sketch, "E5.132.1", {"start": v(42.4, -4.58) * mm, "end": v(41.44, -4.48) * mm});
            skLineSegment(sketch, "E5.132.2", {"start": v(42.42, -4.33) * mm, "end": v(42.4, -4.58) * mm});
            skArc(sketch, "E5.132.3", {"start": v(41.44, -4.48) * mm, "mid": v(41.45, -4.36) * mm, "end": v(41.47, -4.23) * mm});
            skLineSegment(sketch, "E5.133.0", {"start": v(41.59, -2.78) * mm, "end": v(42.54, -2.85) * mm});
            skLineSegment(sketch, "E5.133.1", {"start": v(42.53, -3.1) * mm, "end": v(41.57, -3.03) * mm});
            skLineSegment(sketch, "E5.133.2", {"start": v(42.54, -2.85) * mm, "end": v(42.53, -3.1) * mm});
            skArc(sketch, "E5.133.3", {"start": v(41.57, -3.03) * mm, "mid": v(41.58, -2.9) * mm, "end": v(41.59, -2.78) * mm});
            skLineSegment(sketch, "E5.134.0", {"start": v(41.66, -1.33) * mm, "end": v(42.62, -1.36) * mm});
            skLineSegment(sketch, "E5.134.1", {"start": v(42.6, -1.62) * mm, "end": v(41.65, -1.58) * mm});
            skLineSegment(sketch, "E5.134.2", {"start": v(42.62, -1.36) * mm, "end": v(42.6, -1.62) * mm});
            skArc(sketch, "E5.134.3", {"start": v(41.65, -1.58) * mm, "mid": v(41.66, -1.45) * mm, "end": v(41.66, -1.33) * mm});
            skLineSegment(sketch, "E5.135.0", {"start": v(41.68, 0.13) * mm, "end": v(42.64, 0.13) * mm});
            skLineSegment(sketch, "E5.135.1", {"start": v(42.64, -0.13) * mm, "end": v(41.68, -0.13) * mm});
            skLineSegment(sketch, "E5.135.2", {"start": v(42.64, 0.13) * mm, "end": v(42.64, -0.13) * mm});
            skArc(sketch, "E5.135.3", {"start": v(41.68, -0.13) * mm, "mid": v(41.68, 0) * mm, "end": v(41.68, 0.13) * mm});
            skLineSegment(sketch, "E5.136.0", {"start": v(41.65, 1.58) * mm, "end": v(42.6, 1.62) * mm});
            skLineSegment(sketch, "E5.136.1", {"start": v(42.62, 1.36) * mm, "end": v(41.66, 1.33) * mm});
            skLineSegment(sketch, "E5.136.2", {"start": v(42.6, 1.62) * mm, "end": v(42.62, 1.36) * mm});
            skArc(sketch, "E5.136.3", {"start": v(41.66, 1.33) * mm, "mid": v(41.66, 1.45) * mm, "end": v(41.65, 1.58) * mm});
            skLineSegment(sketch, "E5.137.0", {"start": v(41.57, 3.03) * mm, "end": v(42.53, 3.1) * mm});
            skLineSegment(sketch, "E5.137.1", {"start": v(42.54, 2.85) * mm, "end": v(41.59, 2.78) * mm});
            skLineSegment(sketch, "E5.137.2", {"start": v(42.53, 3.1) * mm, "end": v(42.54, 2.85) * mm});
            skArc(sketch, "E5.137.3", {"start": v(41.59, 2.78) * mm, "mid": v(41.58, 2.9) * mm, "end": v(41.57, 3.03) * mm});
            skLineSegment(sketch, "E5.138.0", {"start": v(41.44, 4.48) * mm, "end": v(42.4, 4.58) * mm});
            skLineSegment(sketch, "E5.138.1", {"start": v(42.42, 4.33) * mm, "end": v(41.47, 4.23) * mm});
            skLineSegment(sketch, "E5.138.2", {"start": v(42.4, 4.58) * mm, "end": v(42.42, 4.33) * mm});
            skArc(sketch, "E5.138.3", {"start": v(41.47, 4.23) * mm, "mid": v(41.45, 4.36) * mm, "end": v(41.44, 4.48) * mm});
            skLineSegment(sketch, "E5.139.0", {"start": v(41.26, 5.93) * mm, "end": v(42.2, 6.06) * mm});
            skLineSegment(sketch, "E5.139.1", {"start": v(42.24, 5.8) * mm, "end": v(41.3, 5.68) * mm});
            skLineSegment(sketch, "E5.139.2", {"start": v(42.2, 6.06) * mm, "end": v(42.24, 5.8) * mm});
            skArc(sketch, "E5.139.3", {"start": v(41.3, 5.68) * mm, "mid": v(41.28, 5.8) * mm, "end": v(41.26, 5.93) * mm});
            skLineSegment(sketch, "E5.140.0", {"start": v(41.03, 7.36) * mm, "end": v(41.97, 7.53) * mm});
            skLineSegment(sketch, "E5.140.1", {"start": v(42.01, 7.28) * mm, "end": v(41.07, 7.11) * mm});
            skLineSegment(sketch, "E5.140.2", {"start": v(41.97, 7.53) * mm, "end": v(42.01, 7.28) * mm});
            skArc(sketch, "E5.140.3", {"start": v(41.07, 7.11) * mm, "mid": v(41.05, 7.24) * mm, "end": v(41.03, 7.36) * mm});
            skLineSegment(sketch, "E5.141.0", {"start": v(40.74, 8.8) * mm, "end": v(41.68, 8.99) * mm});
            skLineSegment(sketch, "E5.141.1", {"start": v(41.73, 8.74) * mm, "end": v(40.8, 8.54) * mm});
            skLineSegment(sketch, "E5.141.2", {"start": v(41.68, 8.99) * mm, "end": v(41.73, 8.74) * mm});
            skArc(sketch, "E5.141.3", {"start": v(40.8, 8.54) * mm, "mid": v(40.77, 8.67) * mm, "end": v(40.74, 8.8) * mm});
            skLineSegment(sketch, "E5.142.0", {"start": v(40.41, 10.2) * mm, "end": v(41.34, 10.44) * mm});
            skLineSegment(sketch, "E5.142.1", {"start": v(41.4, 10.2) * mm, "end": v(40.47, 9.96) * mm});
            skLineSegment(sketch, "E5.142.2", {"start": v(41.34, 10.44) * mm, "end": v(41.4, 10.2) * mm});
            skArc(sketch, "E5.142.3", {"start": v(40.47, 9.96) * mm, "mid": v(40.44, 10.08) * mm, "end": v(40.41, 10.2) * mm});
            skLineSegment(sketch, "E5.143.0", {"start": v(40.03, 11.61) * mm, "end": v(40.95, 11.87) * mm});
            skLineSegment(sketch, "E5.143.1", {"start": v(41.02, 11.63) * mm, "end": v(40.1, 11.37) * mm});
            skLineSegment(sketch, "E5.143.2", {"start": v(40.95, 11.87) * mm, "end": v(41.02, 11.63) * mm});
            skArc(sketch, "E5.143.3", {"start": v(40.1, 11.37) * mm, "mid": v(40.07, 11.49) * mm, "end": v(40.03, 11.61) * mm});
            skLineSegment(sketch, "E5.144.0", {"start": v(39.6, 13) * mm, "end": v(40.51, 13.3) * mm});
            skLineSegment(sketch, "E5.144.1", {"start": v(40.6, 13.06) * mm, "end": v(39.68, 12.76) * mm});
            skLineSegment(sketch, "E5.144.2", {"start": v(40.51, 13.3) * mm, "end": v(40.6, 13.06) * mm});
            skArc(sketch, "E5.144.3", {"start": v(39.68, 12.76) * mm, "mid": v(39.64, 12.88) * mm, "end": v(39.6, 13) * mm});
            skLineSegment(sketch, "E5.145.0", {"start": v(39.12, 14.38) * mm, "end": v(40.02, 14.7) * mm});
            skLineSegment(sketch, "E5.145.1", {"start": v(40.11, 14.46) * mm, "end": v(39.21, 14.14) * mm});
            skLineSegment(sketch, "E5.145.2", {"start": v(40.02, 14.7) * mm, "end": v(40.11, 14.46) * mm});
            skArc(sketch, "E5.145.3", {"start": v(39.21, 14.14) * mm, "mid": v(39.17, 14.26) * mm, "end": v(39.12, 14.38) * mm});
            skLineSegment(sketch, "E5.146.0", {"start": v(38.6, 15.73) * mm, "end": v(39.49, 16.1) * mm});
            skLineSegment(sketch, "E5.146.1", {"start": v(39.58, 15.86) * mm, "end": v(38.7, 15.5) * mm});
            skLineSegment(sketch, "E5.146.2", {"start": v(39.49, 16.1) * mm, "end": v(39.58, 15.86) * mm});
            skArc(sketch, "E5.146.3", {"start": v(38.7, 15.5) * mm, "mid": v(38.65, 15.61) * mm, "end": v(38.6, 15.73) * mm});
            skLineSegment(sketch, "E5.147.0", {"start": v(38.03, 17.07) * mm, "end": v(38.9, 17.46) * mm});
            skLineSegment(sketch, "E5.147.1", {"start": v(39, 17.23) * mm, "end": v(38.13, 16.84) * mm});
            skLineSegment(sketch, "E5.147.2", {"start": v(38.9, 17.46) * mm, "end": v(39, 17.23) * mm});
            skArc(sketch, "E5.147.3", {"start": v(38.13, 16.84) * mm, "mid": v(38.08, 16.95) * mm, "end": v(38.03, 17.07) * mm});
            skLineSegment(sketch, "E5.148.0", {"start": v(37.4, 18.39) * mm, "end": v(38.27, 18.8) * mm});
            skLineSegment(sketch, "E5.148.1", {"start": v(38.38, 18.58) * mm, "end": v(37.52, 18.16) * mm});
            skLineSegment(sketch, "E5.148.2", {"start": v(38.27, 18.8) * mm, "end": v(38.38, 18.58) * mm});
            skArc(sketch, "E5.148.3", {"start": v(37.52, 18.16) * mm, "mid": v(37.46, 18.27) * mm, "end": v(37.4, 18.39) * mm});
            skLineSegment(sketch, "E5.149.0", {"start": v(36.74, 19.68) * mm, "end": v(37.59, 20.13) * mm});
            skLineSegment(sketch, "E5.149.1", {"start": v(37.7, 19.9) * mm, "end": v(36.86, 19.46) * mm});
            skLineSegment(sketch, "E5.149.2", {"start": v(37.59, 20.13) * mm, "end": v(37.7, 19.9) * mm});
            skArc(sketch, "E5.149.3", {"start": v(36.86, 19.46) * mm, "mid": v(36.8, 19.57) * mm, "end": v(36.74, 19.68) * mm});
            skLineSegment(sketch, "E6.1.150.0", {"start": v(36.03, 20.95) * mm, "end": v(36.86, 21.43) * mm});
            skLineSegment(sketch, "E6.3.150.0", {"start": v(36.99, 21.2) * mm, "end": v(36.16, 20.73) * mm});
            skLineSegment(sketch, "E6.6.150.0", {"start": v(36.86, 21.43) * mm, "end": v(36.99, 21.2) * mm});
            skArc(sketch, "E6.9.150.0", {"start": v(36.16, 20.73) * mm, "mid": v(36.1, 20.84) * mm, "end": v(36.03, 20.95) * mm});
            skLineSegment(sketch, "E6.1.151.0", {"start": v(35.28, 22.2) * mm, "end": v(36.1, 22.7) * mm});
            skLineSegment(sketch, "E6.3.151.0", {"start": v(36.23, 22.49) * mm, "end": v(35.41, 21.98) * mm});
            skLineSegment(sketch, "E6.6.151.0", {"start": v(36.1, 22.7) * mm, "end": v(36.23, 22.49) * mm});
            skArc(sketch, "E6.9.151.0", {"start": v(35.41, 21.98) * mm, "mid": v(35.35, 22.09) * mm, "end": v(35.28, 22.2) * mm});
            skLineSegment(sketch, "E6.1.152.0", {"start": v(34.48, 23.41) * mm, "end": v(35.28, 23.95) * mm});
            skLineSegment(sketch, "E6.3.152.0", {"start": v(35.42, 23.74) * mm, "end": v(34.63, 23.2) * mm});
            skLineSegment(sketch, "E6.6.152.0", {"start": v(35.28, 23.95) * mm, "end": v(35.42, 23.74) * mm});
            skArc(sketch, "E6.9.152.0", {"start": v(34.63, 23.2) * mm, "mid": v(34.56, 23.3) * mm, "end": v(34.48, 23.41) * mm});
            skLineSegment(sketch, "E6.1.153.0", {"start": v(33.65, 24.6) * mm, "end": v(34.42, 25.17) * mm});
            skLineSegment(sketch, "E6.3.153.0", {"start": v(34.57, 24.96) * mm, "end": v(33.8, 24.4) * mm});
            skLineSegment(sketch, "E6.6.153.0", {"start": v(34.42, 25.17) * mm, "end": v(34.57, 24.96) * mm});
            skArc(sketch, "E6.9.153.0", {"start": v(33.8, 24.4) * mm, "mid": v(33.72, 24.5) * mm, "end": v(33.65, 24.6) * mm});
            skLineSegment(sketch, "E6.1.154.0", {"start": v(32.77, 25.76) * mm, "end": v(33.52, 26.35) * mm});
            skLineSegment(sketch, "E6.3.154.0", {"start": v(33.68, 26.15) * mm, "end": v(32.92, 25.56) * mm});
            skLineSegment(sketch, "E6.6.154.0", {"start": v(33.52, 26.35) * mm, "end": v(33.68, 26.15) * mm});
            skArc(sketch, "E6.9.154.0", {"start": v(32.92, 25.56) * mm, "mid": v(32.85, 25.66) * mm, "end": v(32.77, 25.76) * mm});
            skLineSegment(sketch, "E6.1.155.0", {"start": v(31.85, 26.89) * mm, "end": v(32.58, 27.5) * mm});
            skLineSegment(sketch, "E6.3.155.0", {"start": v(32.74, 27.31) * mm, "end": v(32.01, 26.7) * mm});
            skLineSegment(sketch, "E6.6.155.0", {"start": v(32.58, 27.5) * mm, "end": v(32.74, 27.31) * mm});
            skArc(sketch, "E6.9.155.0", {"start": v(32.01, 26.7) * mm, "mid": v(31.93, 26.8) * mm, "end": v(31.85, 26.89) * mm});
            skLineSegment(sketch, "E6.1.156.0", {"start": v(30.9, 27.98) * mm, "end": v(31.6, 28.63) * mm});
            skLineSegment(sketch, "E6.3.156.0", {"start": v(31.77, 28.44) * mm, "end": v(31.06, 27.8) * mm});
            skLineSegment(sketch, "E6.6.156.0", {"start": v(31.6, 28.63) * mm, "end": v(31.77, 28.44) * mm});
            skArc(sketch, "E6.9.156.0", {"start": v(31.06, 27.8) * mm, "mid": v(30.98, 27.9) * mm, "end": v(30.9, 27.98) * mm});
            skLineSegment(sketch, "E6.1.157.0", {"start": v(29.9, 29.05) * mm, "end": v(30.58, 29.71) * mm});
            skLineSegment(sketch, "E6.3.157.0", {"start": v(30.76, 29.53) * mm, "end": v(30.07, 28.86) * mm});
            skLineSegment(sketch, "E6.6.157.0", {"start": v(30.58, 29.71) * mm, "end": v(30.76, 29.53) * mm});
            skArc(sketch, "E6.9.157.0", {"start": v(30.07, 28.86) * mm, "mid": v(29.98, 28.95) * mm, "end": v(29.9, 29.05) * mm});
            skLineSegment(sketch, "E6.1.158.0", {"start": v(28.86, 30.07) * mm, "end": v(29.53, 30.76) * mm});
            skLineSegment(sketch, "E6.3.158.0", {"start": v(29.71, 30.58) * mm, "end": v(29.05, 29.9) * mm});
            skLineSegment(sketch, "E6.6.158.0", {"start": v(29.53, 30.76) * mm, "end": v(29.71, 30.58) * mm});
            skArc(sketch, "E6.9.158.0", {"start": v(29.05, 29.9) * mm, "mid": v(28.95, 29.98) * mm, "end": v(28.86, 30.07) * mm});
            skLineSegment(sketch, "E6.1.159.0", {"start": v(27.8, 31.06) * mm, "end": v(28.44, 31.77) * mm});
            skLineSegment(sketch, "E6.3.159.0", {"start": v(28.63, 31.6) * mm, "end": v(27.98, 30.9) * mm});
            skLineSegment(sketch, "E6.6.159.0", {"start": v(28.44, 31.77) * mm, "end": v(28.63, 31.6) * mm});
            skArc(sketch, "E6.9.159.0", {"start": v(27.98, 30.9) * mm, "mid": v(27.9, 30.98) * mm, "end": v(27.8, 31.06) * mm});
            skLineSegment(sketch, "E7.1.160.0", {"start": v(26.7, 32.01) * mm, "end": v(27.31, 32.74) * mm});
            skLineSegment(sketch, "E7.3.160.0", {"start": v(27.5, 32.58) * mm, "end": v(26.89, 31.85) * mm});
            skLineSegment(sketch, "E7.6.160.0", {"start": v(27.31, 32.74) * mm, "end": v(27.5, 32.58) * mm});
            skArc(sketch, "E7.9.160.0", {"start": v(26.89, 31.85) * mm, "mid": v(26.8, 31.93) * mm, "end": v(26.7, 32.01) * mm});
            skLineSegment(sketch, "E7.1.161.0", {"start": v(25.56, 32.92) * mm, "end": v(26.15, 33.68) * mm});
            skLineSegment(sketch, "E7.3.161.0", {"start": v(26.35, 33.52) * mm, "end": v(25.76, 32.77) * mm});
            skLineSegment(sketch, "E7.6.161.0", {"start": v(26.15, 33.68) * mm, "end": v(26.35, 33.52) * mm});
            skArc(sketch, "E7.9.161.0", {"start": v(25.76, 32.77) * mm, "mid": v(25.66, 32.85) * mm, "end": v(25.56, 32.92) * mm});
            skLineSegment(sketch, "E7.1.162.0", {"start": v(24.4, 33.8) * mm, "end": v(24.96, 34.57) * mm});
            skLineSegment(sketch, "E7.3.162.0", {"start": v(25.17, 34.42) * mm, "end": v(24.6, 33.65) * mm});
            skLineSegment(sketch, "E7.6.162.0", {"start": v(24.96, 34.57) * mm, "end": v(25.17, 34.42) * mm});
            skArc(sketch, "E7.9.162.0", {"start": v(24.6, 33.65) * mm, "mid": v(24.5, 33.72) * mm, "end": v(24.4, 33.8) * mm});
            skLineSegment(sketch, "E7.1.163.0", {"start": v(23.2, 34.63) * mm, "end": v(23.74, 35.42) * mm});
            skLineSegment(sketch, "E7.3.163.0", {"start": v(23.95, 35.28) * mm, "end": v(23.41, 34.48) * mm});
            skLineSegment(sketch, "E7.6.163.0", {"start": v(23.74, 35.42) * mm, "end": v(23.95, 35.28) * mm});
            skArc(sketch, "E7.9.163.0", {"start": v(23.41, 34.48) * mm, "mid": v(23.3, 34.56) * mm, "end": v(23.2, 34.63) * mm});
            skLineSegment(sketch, "E7.1.164.0", {"start": v(21.98, 35.41) * mm, "end": v(22.49, 36.23) * mm});
            skLineSegment(sketch, "E7.3.164.0", {"start": v(22.7, 36.1) * mm, "end": v(22.2, 35.28) * mm});
            skLineSegment(sketch, "E7.6.164.0", {"start": v(22.49, 36.23) * mm, "end": v(22.7, 36.1) * mm});
            skArc(sketch, "E7.9.164.0", {"start": v(22.2, 35.28) * mm, "mid": v(22.09, 35.35) * mm, "end": v(21.98, 35.41) * mm});
            skLineSegment(sketch, "E7.1.165.0", {"start": v(20.73, 36.16) * mm, "end": v(21.2, 36.99) * mm});
            skLineSegment(sketch, "E7.3.165.0", {"start": v(21.43, 36.86) * mm, "end": v(20.95, 36.03) * mm});
            skLineSegment(sketch, "E7.6.165.0", {"start": v(21.2, 36.99) * mm, "end": v(21.43, 36.86) * mm});
            skArc(sketch, "E7.9.165.0", {"start": v(20.95, 36.03) * mm, "mid": v(20.84, 36.1) * mm, "end": v(20.73, 36.16) * mm});
            skLineSegment(sketch, "E7.1.166.0", {"start": v(19.46, 36.86) * mm, "end": v(19.9, 37.7) * mm});
            skLineSegment(sketch, "E7.3.166.0", {"start": v(20.13, 37.59) * mm, "end": v(19.68, 36.74) * mm});
            skLineSegment(sketch, "E7.6.166.0", {"start": v(19.9, 37.7) * mm, "end": v(20.13, 37.59) * mm});
            skArc(sketch, "E7.9.166.0", {"start": v(19.68, 36.74) * mm, "mid": v(19.57, 36.8) * mm, "end": v(19.46, 36.86) * mm});
            skLineSegment(sketch, "E7.1.167.0", {"start": v(18.16, 37.52) * mm, "end": v(18.58, 38.38) * mm});
            skLineSegment(sketch, "E7.3.167.0", {"start": v(18.8, 38.27) * mm, "end": v(18.39, 37.4) * mm});
            skLineSegment(sketch, "E7.6.167.0", {"start": v(18.58, 38.38) * mm, "end": v(18.8, 38.27) * mm});
            skArc(sketch, "E7.9.167.0", {"start": v(18.39, 37.4) * mm, "mid": v(18.27, 37.46) * mm, "end": v(18.16, 37.52) * mm});
            skLineSegment(sketch, "E7.1.168.0", {"start": v(16.84, 38.13) * mm, "end": v(17.23, 39) * mm});
            skLineSegment(sketch, "E7.3.168.0", {"start": v(17.46, 38.9) * mm, "end": v(17.07, 38.03) * mm});
            skLineSegment(sketch, "E7.6.168.0", {"start": v(17.23, 39) * mm, "end": v(17.46, 38.9) * mm});
            skArc(sketch, "E7.9.168.0", {"start": v(17.07, 38.03) * mm, "mid": v(16.95, 38.08) * mm, "end": v(16.84, 38.13) * mm});
            skLineSegment(sketch, "E7.1.169.0", {"start": v(15.5, 38.7) * mm, "end": v(15.86, 39.58) * mm});
            skLineSegment(sketch, "E7.3.169.0", {"start": v(16.1, 39.49) * mm, "end": v(15.73, 38.6) * mm});
            skLineSegment(sketch, "E7.6.169.0", {"start": v(15.86, 39.58) * mm, "end": v(16.1, 39.49) * mm});
            skArc(sketch, "E7.9.169.0", {"start": v(15.73, 38.6) * mm, "mid": v(15.61, 38.65) * mm, "end": v(15.5, 38.7) * mm});
            skLineSegment(sketch, "E7.1.170.0", {"start": v(14.14, 39.21) * mm, "end": v(14.46, 40.11) * mm});
            skLineSegment(sketch, "E7.3.170.0", {"start": v(14.7, 40.02) * mm, "end": v(14.38, 39.12) * mm});
            skLineSegment(sketch, "E7.6.170.0", {"start": v(14.46, 40.11) * mm, "end": v(14.7, 40.02) * mm});
            skArc(sketch, "E7.9.170.0", {"start": v(14.38, 39.12) * mm, "mid": v(14.26, 39.17) * mm, "end": v(14.14, 39.21) * mm});
            skLineSegment(sketch, "E7.1.171.0", {"start": v(12.76, 39.68) * mm, "end": v(13.06, 40.6) * mm});
            skLineSegment(sketch, "E7.3.171.0", {"start": v(13.3, 40.51) * mm, "end": v(13, 39.6) * mm});
            skLineSegment(sketch, "E7.6.171.0", {"start": v(13.06, 40.6) * mm, "end": v(13.3, 40.51) * mm});
            skArc(sketch, "E7.9.171.0", {"start": v(13, 39.6) * mm, "mid": v(12.88, 39.64) * mm, "end": v(12.76, 39.68) * mm});
            skLineSegment(sketch, "E7.1.172.0", {"start": v(11.37, 40.1) * mm, "end": v(11.63, 41.02) * mm});
            skLineSegment(sketch, "E7.3.172.0", {"start": v(11.87, 40.95) * mm, "end": v(11.61, 40.03) * mm});
            skLineSegment(sketch, "E7.6.172.0", {"start": v(11.63, 41.02) * mm, "end": v(11.87, 40.95) * mm});
            skArc(sketch, "E7.9.172.0", {"start": v(11.61, 40.03) * mm, "mid": v(11.49, 40.07) * mm, "end": v(11.37, 40.1) * mm});
            skLineSegment(sketch, "E7.1.173.0", {"start": v(9.96, 40.47) * mm, "end": v(10.2, 41.4) * mm});
            skLineSegment(sketch, "E7.3.173.0", {"start": v(10.44, 41.34) * mm, "end": v(10.2, 40.41) * mm});
            skLineSegment(sketch, "E7.6.173.0", {"start": v(10.2, 41.4) * mm, "end": v(10.44, 41.34) * mm});
            skArc(sketch, "E7.9.173.0", {"start": v(10.2, 40.41) * mm, "mid": v(10.08, 40.44) * mm, "end": v(9.96, 40.47) * mm});
            skLineSegment(sketch, "E7.1.174.0", {"start": v(8.54, 40.8) * mm, "end": v(8.74, 41.73) * mm});
            skLineSegment(sketch, "E7.3.174.0", {"start": v(8.99, 41.68) * mm, "end": v(8.8, 40.74) * mm});
            skLineSegment(sketch, "E7.6.174.0", {"start": v(8.74, 41.73) * mm, "end": v(8.99, 41.68) * mm});
            skArc(sketch, "E7.9.174.0", {"start": v(8.8, 40.74) * mm, "mid": v(8.67, 40.77) * mm, "end": v(8.54, 40.8) * mm});
            skLineSegment(sketch, "E7.1.175.0", {"start": v(7.11, 41.07) * mm, "end": v(7.28, 42.01) * mm});
            skLineSegment(sketch, "E7.3.175.0", {"start": v(7.53, 41.97) * mm, "end": v(7.36, 41.03) * mm});
            skLineSegment(sketch, "E7.6.175.0", {"start": v(7.28, 42.01) * mm, "end": v(7.53, 41.97) * mm});
            skArc(sketch, "E7.9.175.0", {"start": v(7.36, 41.03) * mm, "mid": v(7.24, 41.05) * mm, "end": v(7.11, 41.07) * mm});
            skLineSegment(sketch, "E7.1.176.0", {"start": v(5.68, 41.3) * mm, "end": v(5.8, 42.24) * mm});
            skLineSegment(sketch, "E7.3.176.0", {"start": v(6.06, 42.2) * mm, "end": v(5.93, 41.26) * mm});
            skLineSegment(sketch, "E7.6.176.0", {"start": v(5.8, 42.24) * mm, "end": v(6.06, 42.2) * mm});
            skArc(sketch, "E7.9.176.0", {"start": v(5.93, 41.26) * mm, "mid": v(5.8, 41.28) * mm, "end": v(5.68, 41.3) * mm});
            skLineSegment(sketch, "E7.1.177.0", {"start": v(4.23, 41.47) * mm, "end": v(4.33, 42.42) * mm});
            skLineSegment(sketch, "E7.3.177.0", {"start": v(4.58, 42.4) * mm, "end": v(4.48, 41.44) * mm});
            skLineSegment(sketch, "E7.6.177.0", {"start": v(4.33, 42.42) * mm, "end": v(4.58, 42.4) * mm});
            skArc(sketch, "E7.9.177.0", {"start": v(4.48, 41.44) * mm, "mid": v(4.36, 41.45) * mm, "end": v(4.23, 41.47) * mm});
            skLineSegment(sketch, "E7.1.178.0", {"start": v(2.78, 41.59) * mm, "end": v(2.85, 42.54) * mm});
            skLineSegment(sketch, "E7.3.178.0", {"start": v(3.1, 42.53) * mm, "end": v(3.03, 41.57) * mm});
            skLineSegment(sketch, "E7.6.178.0", {"start": v(2.85, 42.54) * mm, "end": v(3.1, 42.53) * mm});
            skArc(sketch, "E7.9.178.0", {"start": v(3.03, 41.57) * mm, "mid": v(2.9, 41.58) * mm, "end": v(2.78, 41.59) * mm});
            skLineSegment(sketch, "E7.1.179.0", {"start": v(1.33, 41.66) * mm, "end": v(1.36, 42.62) * mm});
            skLineSegment(sketch, "E7.3.179.0", {"start": v(1.62, 42.6) * mm, "end": v(1.58, 41.65) * mm});
            skLineSegment(sketch, "E7.6.179.0", {"start": v(1.36, 42.62) * mm, "end": v(1.62, 42.6) * mm});
            skArc(sketch, "E7.9.179.0", {"start": v(1.58, 41.65) * mm, "mid": v(1.45, 41.66) * mm, "end": v(1.33, 41.66) * mm});
            skSolve(sketch);
        }
        {
            var Q0;
            Q0 = qSketchRegion(id + "F3", true);
            extrude(context, id + "F4", {"entities" : qUnion([Q0]), "operationType" : NewBodyOperationType.REMOVE, "endBound" : BoundingType.THROUGH_ALL, "oppositeDirection" : true, "depth" : 25.4 * mm});
        }
    });
